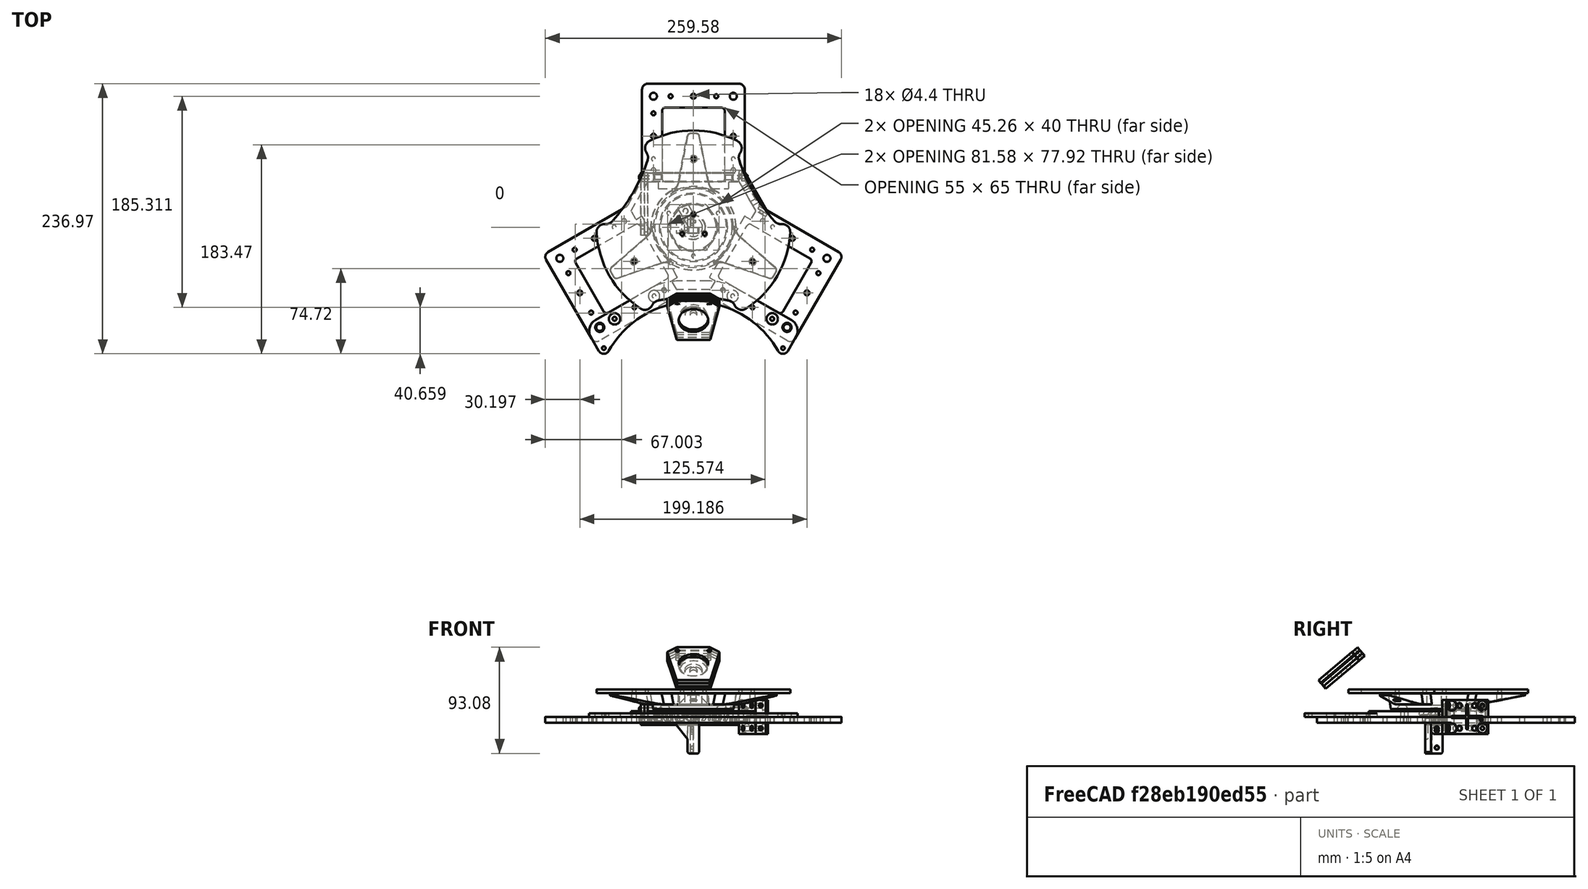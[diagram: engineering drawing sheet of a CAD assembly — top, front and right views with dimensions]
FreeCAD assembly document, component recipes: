
FREECAD ASSEMBLY — COMPONENT RECIPES ("structures")

This assembly document has 14 components, labeled P0..P13 below (a component is one placed body or linked part). 12 of them carry a construction recipe — the FreeCAD feature program that regenerates the part from scratch, quoted from this document or its linked companion documents; the rest are supplied as boundary geometry only. No exploded tour is included for this assembly.
NOTE — this tour is split across 2 documents so each fits a 32k-token context. This is document 1: the component sections continue in the remaining 1 document, each repeating the header above.
COMPONENT P0 — recipe-attached ("PlaqueIntermediaire", modeled in this document).
Construction recipe (the document's own serialized feature program — sketch geometry with constraints, then the solid features built on it; lengths are millimeters unless a unit is written):

FEATURE [Sketcher::SketchObject] Sketch043
  ArcFitTolerance = 0
  AttachmentSupport = -> [XY_Plane031]
  ExternalBSplineMaxDegree = 0
  ExternalBSplineTolerance = 0
  FullyConstrained = true
  InternalTolerance = 1e-06
  InvalidShape = false
  MakeInternals = false
  MapMode = 5
  Support = -> [XY_Plane031]
  TreeRank = 0
  ValidateShape = true
  sketch-geometry (13):
    g0: LineSegment StartX=0 StartY=0 StartZ=0 EndX=0 EndY=-54.641 EndZ=0
    g1: LineSegment StartX=0 StartY=-54.641 StartZ=0 EndX=-14.641 EndY=-54.641 EndZ=0
    g2: LineSegment StartX=-14.641 StartY=-54.641 StartZ=0 EndX=-19.641 EndY=-45.9808 EndZ=0
    g3: LineSegment StartX=-19.641 StartY=-45.9808 StartZ=0 EndX=-28.3013 EndY=-50.9808 EndZ=0
    g4: LineSegment StartX=-28.3013 StartY=-50.9808 StartZ=0 EndX=-58.3013 EndY=0.980762 EndZ=0
    g5: LineSegment StartX=-58.3013 StartY=0.980762 StartZ=0 EndX=-49.641 EndY=5.98076 EndZ=0
    g6: LineSegment StartX=-49.641 StartY=5.98076 StartZ=0 EndX=-54.641 EndY=14.641 EndZ=0
    g7: LineSegment StartX=-54.641 StartY=14.641 StartZ=0 EndX=-47.3205 EndY=27.3205 EndZ=0
    g8: LineSegment StartX=-47.3205 StartY=27.3205 StartZ=0 EndX=0 EndY=0 EndZ=0
    g9: LineSegment [constr] StartX=-49.641 StartY=5.98076 StartZ=0 EndX=-19.641 EndY=-45.9808 EndZ=0
    g10: Circle CenterX=-43.4808 CenterY=15.3109 CenterZ=0 NormalX=0 NormalY=0 NormalZ=1 AngleXU=0 Radius=1.6
    g11: Circle CenterX=-8.48076 CenterY=-45.3109 CenterZ=0 NormalX=0 NormalY=0 NormalZ=1 AngleXU=0 Radius=1.6
    g12: LineSegment [constr] StartX=0 StartY=0 StartZ=0 EndX=-43.3013 EndY=-25 EndZ=0
  constraints (35):
    c: Coincident(g0,g-1)
    c: PointOnObject(g0,g-2)
    c: Coincident(g1,g0)
    c: Horizontal(g1)
    c: Coincident(g1,g2)
    c: Coincident(g2,g3)
    c: Coincident(g3,g4)
    c: Coincident(g4,g5)
    c: Coincident(g5,g6)
    c: Coincident(g6,g7)
    c: Coincident(g7,g8)
    c: Coincident(g8,g0)
    c: Angle(g8,g0) = 2.0944
    c: Perpendicular(g7,g8)
    c: Perpendicular(g3,g2)
    c: Perpendicular(g4,g3)
    c: Perpendicular(g4,g5)
    c: Perpendicular(g6,g5)
    c: Equal(g7,g1)
    c: Coincident(g9,g5)
    c: Tangent(g9,g2) = 1.5708
    c: Equal(g2,g3)
    c: Equal(g5,g6)
    c: Distance(g6) = 10
    c: Equal(g0,g8)
    c: Distance(g4) = 60
    c: Distance(g0,g9) = 40
    c: Coincident(g12,g0)
    c: PointOnObject(g12,g4)
    c: Perpendicular(g4,g12)
    c: Symmetric(g11,g10,g12)
    c: Diameter(g10) = 3.2
    c: Equal(g10,g11)
    c: Distance(g11,g2) = 10
    c: Distance(g11,g12) = 35
FEATURE [PartDesign::Pad] Pad027
  AddSubType = 0
  AutoTaperInnerAngle = false
  CheckUpToFaceLimits = true
  ClaimChildren = false
  Direction = (1,1,1)
  Fit = 0
  FitJoin = 0
  InnerFit = 0
  InnerFitJoin = 0
  InvalidShape = false
  Length = 5
  Length2 = 100
  Linearize = true
  NewSolid = false
  Profile = -> Sketch043
  Refine = true
  Suppress = false
  TaperInnerAngle = 0
  TaperInnerAngleRev = 0
  TreeRank = 0
  Type = 0
  ValidateShape = true
  _ProfileBasedVersion = 1
FEATURE [PartDesign::PolarPattern] PolarPattern014
  AddSubType = 0
  Angle = 360
  Axis = -> Sketch043 [N_Axis]
  BaseFeature = -> Pad027
  CopyShape = false
  InvalidShape = false
  NewSolid = false
  Occurrences = 3
  OriginalSubs = -> [Pad027]
  Originals = -> [Pad027]
  ParallelTransform = true
  Refine = true
  SubTransform = true
  Suppress = false
  TreeRank = 0
  ValidateShape = true
  _Version = 2
FEATURE [Sketcher::SketchObject] Sketch044
  ArcFitTolerance = 0
  AttachmentSupport = -> [XY_Plane031]
  ExternalBSplineMaxDegree = 0
  ExternalBSplineTolerance = 0
  FullyConstrained = true
  InternalTolerance = 1e-06
  InvalidShape = false
  MakeInternals = false
  MapMode = 5
  Support = -> [XY_Plane031]
  TreeRank = 0
  ValidateShape = true
  sketch-geometry (5):
    g0: LineSegment StartX=-35.6218 StartY=8.30127 StartZ=0 EndX=-10.6218 EndY=-35 EndZ=0
    g1: LineSegment StartX=-10.6218 StartY=-35 StartZ=0 EndX=0 EndY=-35 EndZ=0
    g2: LineSegment StartX=0 StartY=-35 StartZ=0 EndX=0 EndY=0 EndZ=0
    g3: LineSegment StartX=0 StartY=0 StartZ=0 EndX=-30.3109 EndY=17.5 EndZ=0
    g4: LineSegment StartX=-30.3109 StartY=17.5 StartZ=0 EndX=-35.6218 EndY=8.30127 EndZ=0
  constraints (14):
    c: Coincident(g0,g1)
    c: PointOnObject(g1,g-2)
    c: Horizontal(g1)
    c: Coincident(g1,g2)
    c: Coincident(g2,g-1)
    c: Coincident(g2,g3)
    c: Coincident(g3,g4)
    c: Coincident(g4,g0)
    c: Perpendicular(g4,g3)
    c: Equal(g4,g1)
    c: Equal(g2,g3)
    c: Angle(g3,g2) = 2.0944
    c: Distance(g0) = 50
    c: DistanceY(g2,g2) = 35
FEATURE [PartDesign::Pocket] Pocket017
  AddSubType = 1
  AutoTaperInnerAngle = false
  BaseFeature = -> PolarPattern014
  CheckUpToFaceLimits = true
  ClaimChildren = false
  Direction = (1,1,1)
  Fit = 0
  FitJoin = 0
  InnerFit = 0
  InnerFitJoin = 0
  InvalidShape = false
  Length = 5
  Length2 = 100
  Linearize = true
  NewSolid = false
  Profile = -> Sketch044
  Refine = true
  Reversed = true
  Suppress = false
  TaperInnerAngle = 0
  TaperInnerAngleRev = 0
  TreeRank = 0
  Type = 1
  ValidateShape = true
  _ProfileBasedVersion = 1
  _Version = 0
FEATURE [PartDesign::PolarPattern] PolarPattern015
  AddSubType = 0
  Angle = 360
  Axis = -> Sketch044 [N_Axis]
  BaseFeature = -> Pocket017
  CopyShape = false
  InvalidShape = false
  NewSolid = false
  Occurrences = 3
  OriginalSubs = -> [Pocket017]
  Originals = -> [Pocket017]
  ParallelTransform = true
  Refine = true
  SubTransform = true
  Suppress = false
  TreeRank = 0
  ValidateShape = true
  _Version = 2
FEATURE [PartDesign::Chamfer] Chamfer007
  AddSubType = 0
  Angle = 45
  Base = -> PolarPattern015 [Edge8,Edge66,Edge67,Edge68,Edge77,Edge78]
  BaseFeature = -> PolarPattern015
  ChamferType = 0
  FlipDirection = false
  InvalidShape = false
  NewSolid = false
  Refine = true
  Size = 1
  Size2 = 1
  SupportTransform = false
  Suppress = false
  TreeRank = 0
  UseAllEdges = false
  ValidateShape = true
FEATURE [PartDesign::Fillet] Fillet014
  AddSubType = 0
  Base = -> Chamfer007 [Edge101,Edge103,Edge104,Edge105,Edge106,Edge102]
  BaseFeature = -> Chamfer007
  InvalidShape = false
  NewSolid = false
  Radius = 3
  Refine = true
  SupportTransform = false
  Suppress = false
  TreeRank = 0
  UseAllEdges = false
  ValidateShape = true
FEATURE [PartDesign::Body] Body024  label="PlaqueIntermediaire"
  AutoGroupSolids = false
  ClaimAllChildren = false
  ExportMode = 0
  Group = -> [Sketch043,Pad027,PolarPattern014,Sketch044,Pocket017,PolarPattern015,Chamfer007,Fillet014]
  InvalidShape = false
  Origin = -> Origin036
  SingleSolid = true
  Tip = -> Fillet014
  TreeRank = 0
  ValidateShape = true
  _ExportChildren = -> [Pad027,PolarPattern014,Pocket017,PolarPattern015,Chamfer007,Fillet014]
  _GroupVersion = 1
COMPONENT P1 — recipe-attached ("CoinStandard", modeled in this document).
Construction recipe (the document's own serialized feature program — sketch geometry with constraints, then the solid features built on it; lengths are millimeters unless a unit is written):

FEATURE [Sketcher::SketchObject] Sketch060
  ArcFitTolerance = 0
  AttachmentSupport = -> [XY_Plane037]
  ExternalBSplineMaxDegree = 0
  ExternalBSplineTolerance = 0
  FullyConstrained = true
  InternalTolerance = 1e-06
  InvalidShape = false
  MakeInternals = false
  MapMode = 5
  Support = -> [XY_Plane037]
  TreeRank = 0
  ValidateShape = true
  sketch-geometry (10):
    g0: LineSegment [constr] StartX=0 StartY=0 StartZ=0 EndX=34.641 EndY=-20 EndZ=0
    g1: LineSegment [constr] StartX=0 StartY=0 StartZ=0 EndX=-34.641 EndY=-20 EndZ=0
    g2: LineSegment [constr] StartX=-34.641 StartY=-20 StartZ=0 EndX=-14.641 EndY=-54.641 EndZ=0
    g3: LineSegment [constr] StartX=34.641 StartY=-20 StartZ=0 EndX=14.641 EndY=-54.641 EndZ=0
    g4: LineSegment StartX=-14.641 StartY=-54.641 StartZ=0 EndX=-23.3013 EndY=-59.641 EndZ=0
    g5: LineSegment StartX=14.641 StartY=-54.641 StartZ=0 EndX=23.3013 EndY=-59.641 EndZ=0
    g6: LineSegment StartX=-23.3013 StartY=-59.641 StartZ=0 EndX=-15 EndY=-89.641 EndZ=0
    g7: LineSegment StartX=23.3013 StartY=-59.641 StartZ=0 EndX=15 EndY=-89.641 EndZ=0
    g8: LineSegment StartX=-14.641 StartY=-54.641 StartZ=0 EndX=14.641 EndY=-54.641 EndZ=0
    g9: LineSegment StartX=-15 StartY=-89.641 StartZ=0 EndX=15 EndY=-89.641 EndZ=0
  constraints (24):
    c: Coincident(g0,g-1)
    c: Coincident(g1,g0)
    c: Symmetric(g0,g1,g-2)
    c: Angle(g1,g0) = 2.0944
    c: Coincident(g2,g1)
    c: Perpendicular(g1,g2)
    c: Coincident(g3,g0)
    c: Symmetric(g3,g2,g-2)
    c: Distance(g2) = 40
    c: Distance(g0) = 40
    c: Coincident(g4,g2)
    c: Coincident(g5,g3)
    c: Perpendicular(g3,g5)
    c: Symmetric(g4,g5,g-2)
    c: Distance(g5) = 10
    c: Coincident(g6,g4)
    c: Coincident(g7,g5)
    c: Symmetric(g7,g6,g-2)
    c: DistanceY(g7,g3) = 35
    c: Coincident(g8,g4)
    c: Coincident(g8,g5)
    c: Coincident(g9,g6)
    c: Coincident(g9,g7)
    c: DistanceX(g9,g9) = 30
FEATURE [PartDesign::Pad] Pad034
  AddSubType = 0
  AutoTaperInnerAngle = false
  CheckUpToFaceLimits = true
  ClaimChildren = false
  Direction = (1,1,1)
  Fit = 0
  FitJoin = 0
  InnerFit = 0
  InnerFitJoin = 0
  InvalidShape = false
  Length = 50
  Length2 = 100
  Linearize = true
  NewSolid = false
  Profile = -> Sketch060
  Refine = true
  Suppress = false
  TaperInnerAngle = 0
  TaperInnerAngleRev = 0
  TreeRank = 0
  Type = 0
  ValidateShape = true
  _ProfileBasedVersion = 1
FEATURE [Sketcher::SketchObject] Sketch061
  ArcFitTolerance = 0
  AttachmentSupport = -> [YZ_Plane037]
  ExternalBSplineMaxDegree = 0
  ExternalBSplineTolerance = 0
  ExternalGeometry = -> [Pad034]
  FullyConstrained = true
  InternalTolerance = 1e-06
  InvalidShape = false
  MakeInternals = false
  MapMode = 5
  Placement = pos=(0,0,0) rot=(0.57735,0.57735,0.57735;2.0944rad)
  Support = -> [YZ_Plane037]
  TreeRank = 0
  ValidateShape = true
  sketch-geometry (4):
    g0: LineSegment StartX=-62.641 StartY=0 StartZ=0 EndX=-89.641 EndY=20.6315 EndZ=0
    g1: LineSegment StartX=-62.641 StartY=0 StartZ=0 EndX=-89.641 EndY=0 EndZ=0
    g2: LineSegment StartX=-89.641 StartY=0 StartZ=0 EndX=-89.641 EndY=20.6315 EndZ=0
    g3: LineSegment [constr] StartX=-89.641 StartY=20.6315 StartZ=0 EndX=-54.641 EndY=50 EndZ=0
  constraints (11):
    c: PointOnObject(g0,g-4)
    c: PointOnObject(g0,g-1)
    c: DistanceX(g0,g-3) = 3
    c: Coincident(g0,g1)
    c: PointOnObject(g1,g-4)
    c: Horizontal(g1)
    c: Coincident(g1,g2)
    c: Coincident(g2,g0)
    c: Coincident(g3,g0)
    c: Coincident(g3,g-5)
    c: Angle(g-4,g3) = 2.26893
FEATURE [PartDesign::Pocket] Pocket025
  AddSubType = 1
  AutoTaperInnerAngle = false
  BaseFeature = -> Pad034
  CheckUpToFaceLimits = true
  ClaimChildren = false
  Direction = (1,1,1)
  Fit = 0
  FitJoin = 0
  InnerFit = 0
  InnerFitJoin = 0
  InvalidShape = false
  Length = 5
  Length2 = 100
  Linearize = true
  Midplane = true
  NewSolid = false
  Profile = -> Sketch061
  Refine = true
  Suppress = false
  TaperInnerAngle = 0
  TaperInnerAngleRev = 0
  TreeRank = 0
  Type = 1
  ValidateShape = true
  _ProfileBasedVersion = 1
  _Version = 1
FEATURE [Sketcher::SketchObject] Sketch062
  ArcFitTolerance = 0
  AttachmentSupport = -> [YZ_Plane037]
  ExternalBSplineMaxDegree = 0
  ExternalBSplineTolerance = 0
  ExternalGeometry = -> [Pocket025]
  FullyConstrained = true
  InternalTolerance = 1e-06
  InvalidShape = false
  MakeInternals = false
  MapMode = 5
  Placement = pos=(0,0,0) rot=(0.57735,0.57735,0.57735;2.0944rad)
  Support = -> [YZ_Plane037]
  TreeRank = 0
  ValidateShape = true
  sketch-geometry (3):
    g0: LineSegment StartX=-89.641 StartY=50 StartZ=0 EndX=-89.641 EndY=20.6315 EndZ=0
    g1: LineSegment StartX=-89.641 StartY=20.6315 StartZ=0 EndX=-54.641 EndY=50 EndZ=0
    g2: LineSegment StartX=-89.641 StartY=50 StartZ=0 EndX=-54.641 EndY=50 EndZ=0
  constraints (6):
    c: Coincident(g1,g0)
    c: Coincident(g-3,g0)
    c: Coincident(g-3,g0)
    c: Coincident(g2,g0)
    c: Coincident(g2,g1)
    c: Coincident(g1,g-5)
FEATURE [PartDesign::Pocket] Pocket026
  AddSubType = 1
  AutoTaperInnerAngle = false
  BaseFeature = -> Pocket025
  CheckUpToFaceLimits = true
  ClaimChildren = false
  Direction = (1,1,1)
  Fit = 0
  FitJoin = 0
  InnerFit = 0
  InnerFitJoin = 0
  InvalidShape = false
  Length = 5
  Length2 = 100
  Linearize = true
  Midplane = true
  NewSolid = false
  Profile = -> Sketch062
  Refine = true
  Suppress = false
  TaperInnerAngle = 0
  TaperInnerAngleRev = 0
  TreeRank = 0
  Type = 1
  ValidateShape = true
  _ProfileBasedVersion = 1
  _Version = 1
FEATURE [PartDesign::Plane] DatumPlane
  AttachmentOffset = pos=(0,0,-30) rot=(0,0,1;0rad)
  AttachmentSupport = -> [Pocket026]
  InvalidShape = false
  Length = 68.3013
  MapMode = 5
  MinimumLength = 10
  MinimumWidth = 10
  Placement = pos=(-35,-60.6218,3.3e-15) rot=(0.186157,0.694747,0.694747;2.77349rad)
  ResizeMode = 0
  Support = -> [Pocket026]
  TreeRank = 0
  ValidateShape = true
  Width = 10
FEATURE [Sketcher::SketchObject] Sketch063
  ArcFitTolerance = 0
  AttachmentSupport = -> [DatumPlane]
  ExternalBSplineMaxDegree = 0
  ExternalBSplineTolerance = 0
  ExternalGeometry = -> [Pocket026]
  FullyConstrained = true
  InternalTolerance = 1e-06
  InvalidShape = false
  MakeInternals = false
  MapMode = 5
  Placement = pos=(-35,-60.6218,3.3e-15) rot=(0.186157,0.694747,0.694747;2.77349rad)
  Support = -> [DatumPlane]
  TreeRank = 0
  ValidateShape = true
  sketch-geometry (2):
    g0: Circle CenterX=-45 CenterY=10 CenterZ=0 NormalX=0 NormalY=0 NormalZ=1 AngleXU=0 Radius=1.6
    g1: LineSegment [constr] StartX=-50 StartY=10 StartZ=0 EndX=-40 EndY=10 EndZ=0
  constraints (6):
    c: PointOnObject(g1,g-3)
    c: PointOnObject(g1,g-4)
    c: Horizontal(g1)
    c: Symmetric(g1,g1,g0)
    c: Diameter(g0) = 3.2
    c: Distance(g-3,g1) = 10
FEATURE [PartDesign::Hole] Hole001
  AddSubType = 1
  BaseFeature = -> Pocket026
  ClaimChildren = false
  CustomThreadClearance = 0
  Depth = 39
  DepthType = 0
  Diameter = 3.2
  DrillForDepth = false
  DrillPoint = 1
  DrillPointAngle = 118
  Fit = 0
  FitJoin = 0
  HoleCutCountersinkAngle = 90
  HoleCutCustomValues = true
  HoleCutDepth = 27
  HoleCutDiameter = 8
  HoleCutType = 1
  InnerFit = 0
  InnerFitJoin = 0
  InvalidShape = false
  ModelThread = false
  NewSolid = false
  Profile = -> Sketch063
  Refine = true
  Reversed = true
  Suppress = false
  Tapered = false
  TaperedAngle = 90
  ThreadClass = 0
  ThreadDepth = 39
  ThreadDepthType = 0
  ThreadDirection = 0
  ThreadFit = 0
  ThreadSize = 0
  ThreadType = 0
  Threaded = false
  TreeRank = 0
  UseCustomThreadClearance = false
  ValidateShape = true
  _ProfileBasedVersion = 1
FEATURE [PartDesign::Mirrored] Mirrored006
  AddSubType = 0
  BaseFeature = -> Hole001
  CopyShape = false
  InvalidShape = false
  MirrorPlane = -> YZ_Plane037
  NewSolid = false
  OriginalSubs = -> [Hole001]
  Originals = -> [Hole001]
  ParallelTransform = true
  Refine = true
  SubTransform = true
  Suppress = false
  TreeRank = 0
  ValidateShape = true
  _Version = 3
FEATURE [Sketcher::SketchObject] Sketch064
  ArcFitTolerance = 0
  AttachmentSupport = -> [Mirrored006]
  ExternalBSplineMaxDegree = 0
  ExternalBSplineTolerance = 0
  ExternalGeometry = -> [Mirrored006]
  FullyConstrained = true
  InternalTolerance = 1e-06
  InvalidShape = false
  MakeInternals = false
  MapMode = 5
  Placement = pos=(-2.64e-14,-47.1965,56.2467) rot=(1,0,0;0.698132rad)
  Support = -> [Mirrored006]
  TreeRank = 0
  ValidateShape = true
  sketch-geometry (2):
    g0: Circle CenterX=-14 CenterY=-14.7181 CenterZ=0 NormalX=0 NormalY=0 NormalZ=1 AngleXU=0 Radius=2.05
    g1: Circle CenterX=14 CenterY=-14.7181 CenterZ=0 NormalX=0 NormalY=0 NormalZ=1 AngleXU=0 Radius=2.05
  constraints (5):
    c: Symmetric(g1,g0,g-2)
    c: Diameter(g0) = 4.1
    c: Equal(g0,g1)
    c: DistanceX(g0,g1) = 28
    c: DistanceY(g0,g-3) = 5
FEATURE [PartDesign::Pocket] Pocket027
  AddSubType = 1
  AutoTaperInnerAngle = false
  BaseFeature = -> Mirrored006
  CheckUpToFaceLimits = true
  ClaimChildren = false
  Direction = (1,1,1)
  Fit = 0
  FitJoin = 0
  InnerFit = 0
  InnerFitJoin = 0
  InvalidShape = false
  Length = 5
  Length2 = 100
  Linearize = true
  NewSolid = false
  Profile = -> Sketch064
  Refine = true
  Suppress = false
  TaperInnerAngle = 0
  TaperInnerAngleRev = 0
  TreeRank = 0
  Type = 1
  ValidateShape = true
  _ProfileBasedVersion = 1
  _Version = 1
FEATURE [Sketcher::SketchObject] Sketch065
  ArcFitTolerance = 0
  AttachmentSupport = -> [Pocket027]
  ExternalBSplineMaxDegree = 0
  ExternalBSplineTolerance = 0
  ExternalGeometry = -> [Pocket027]
  FullyConstrained = true
  InternalTolerance = 1e-06
  InvalidShape = false
  MakeInternals = false
  MapMode = 5
  Placement = pos=(-2.64e-14,-47.1965,56.2467) rot=(1,0,0;0.698132rad)
  Support = -> [Pocket027]
  TreeRank = 0
  ValidateShape = true
  sketch-geometry (3):
    g0: Circle CenterX=0 CenterY=-32.5627 CenterZ=0 NormalX=0 NormalY=0 NormalZ=1 AngleXU=0 Radius=15
    g1: GeomPoint [constr] X=2e-16 Y=-55.4073 Z=0
    g2: GeomPoint [constr] X=0 Y=-9.71807 Z=0
  constraints (6):
    c: PointOnObject(g0,g-2)
    c: Diameter(g0) = 30
    c: PointOnObject(g2,g-2)
    c: PointOnObject(g2,g-3)
    c: PointOnObject(g1,g-4)
    c: Symmetric(g1,g2,g0)
FEATURE [PartDesign::Pocket] Pocket028
  AddSubType = 1
  AutoTaperInnerAngle = false
  BaseFeature = -> Pocket027
  CheckUpToFaceLimits = true
  ClaimChildren = false
  Direction = (1,1,1)
  Fit = 0
  FitJoin = 0
  InnerFit = 0
  InnerFitJoin = 0
  InvalidShape = false
  Length = 17
  Length2 = 100
  Linearize = true
  NewSolid = false
  Profile = -> Sketch065
  Refine = true
  Suppress = false
  TaperInnerAngle = 0
  TaperInnerAngleRev = 0
  TreeRank = 0
  Type = 0
  ValidateShape = true
  _ProfileBasedVersion = 1
  _Version = 1
FEATURE [Sketcher::SketchObject] Sketch066
  ArcFitTolerance = 0
  AttachmentSupport = -> [Pocket028]
  ExternalBSplineMaxDegree = 0
  ExternalBSplineTolerance = 0
  ExternalGeometry = -> [Pocket028]
  FullyConstrained = true
  InternalTolerance = 1e-06
  InvalidShape = false
  MakeInternals = false
  MapMode = 5
  Placement = pos=(-2.64e-14,-47.1965,56.2467) rot=(1,0,0;0.698132rad)
  Support = -> [Pocket028]
  TreeRank = 0
  ValidateShape = true
  sketch-geometry (4):
    g0: ArcOfCircle CenterX=0 CenterY=-32.5627 CenterZ=0 NormalX=0 NormalY=0 NormalZ=1 AngleXU=0 Radius=11.5 StartAngle=3.22982 EndAngle=6.19496
    g1: LineSegment StartX=-11.4553 StartY=-33.576 StartZ=0 EndX=-12.3039 EndY=-23.9828 EndZ=0
    g2: LineSegment StartX=12.3039 StartY=-23.9828 StartZ=0 EndX=11.4553 EndY=-33.576 EndZ=0
    g3: LineSegment StartX=-12.3039 StartY=-23.9828 StartZ=0 EndX=12.3039 EndY=-23.9828 EndZ=0
  constraints (8):
    c: Coincident(g0,g-3)
    c: Diameter(g0) = 23
    c: Coincident(g1,g-4)
    c: Coincident(g2,g-4)
    c: Coincident(g3,g1)
    c: Coincident(g3,g2)
    c: Tangent(g1,g0) = 1.5708
    c: Tangent(g2,g0) = 1.5708
FEATURE [PartDesign::Pocket] Pocket029
  AddSubType = 1
  AutoTaperInnerAngle = false
  BaseFeature = -> Pocket028
  CheckUpToFaceLimits = true
  ClaimChildren = false
  Direction = (1,1,1)
  Fit = 0
  FitJoin = 0
  InnerFit = 0
  InnerFitJoin = 0
  InvalidShape = false
  Length = 5
  Length2 = 100
  Linearize = true
  NewSolid = false
  Profile = -> Sketch066
  Refine = true
  Suppress = false
  TaperInnerAngle = 0
  TaperInnerAngleRev = 0
  TreeRank = 0
  Type = 1
  ValidateShape = true
  _ProfileBasedVersion = 1
  _Version = 1
FEATURE [PartDesign::Chamfer] Chamfer018
  AddSubType = 0
  Angle = 45
  Base = -> Pocket029 [Edge44,Edge31]
  BaseFeature = -> Pocket029
  ChamferType = 0
  FlipDirection = false
  InvalidShape = false
  NewSolid = false
  Refine = true
  Size = 0.4
  Size2 = 1
  SupportTransform = false
  Suppress = false
  TreeRank = 0
  UseAllEdges = false
  ValidateShape = true
FEATURE [PartDesign::Pad] Pad036
  AddSubType = 0
  AutoTaperInnerAngle = false
  BaseFeature = -> Chamfer018
  CheckUpToFaceLimits = true
  ClaimChildren = false
  Direction = (1,1,1)
  Fit = 0
  FitJoin = 0
  InnerFit = 0
  InnerFitJoin = 0
  InvalidShape = false
  Length = 5
  Length2 = 100
  Linearize = true
  NewSolid = false
  Profile = -> Chamfer018 [Face5]
  Refine = true
  Suppress = false
  TaperInnerAngle = 0
  TaperInnerAngleRev = 0
  TreeRank = 0
  Type = 0
  ValidateShape = true
  _ProfileBasedVersion = 1
FEATURE [PartDesign::Chamfer] Chamfer022
  AddSubType = 0
  Angle = 45
  Base = -> Pad036 [Face15]
  BaseFeature = -> Pad036
  ChamferType = 0
  FlipDirection = false
  InvalidShape = false
  NewSolid = false
  Refine = true
  Size = 0.4
  Size2 = 1
  SupportTransform = false
  Suppress = false
  TreeRank = 0
  UseAllEdges = false
  ValidateShape = true
FEATURE [PartDesign::Chamfer] Chamfer023
  AddSubType = 0
  Angle = 45
  Base = -> Chamfer022 [Edge64,Edge63]
  BaseFeature = -> Chamfer022
  ChamferType = 0
  FlipDirection = false
  InvalidShape = false
  NewSolid = false
  Refine = true
  Size = 1
  Size2 = 1
  SupportTransform = false
  Suppress = false
  TreeRank = 0
  UseAllEdges = false
  ValidateShape = true
FEATURE [PartDesign::Body] Body029  label="CoinStandard"
  AutoGroupSolids = false
  ClaimAllChildren = false
  ExportMode = 0
  Group = -> [Sketch060,Pad034,Sketch061,Pocket025,Sketch062,Pocket026,DatumPlane,Sketch063,Hole001,Mirrored006,Sketch064,Pocket027,Sketch065,Pocket028,Sketch066,Pocket029,Chamfer018,Pad036,Chamfer022,Chamfer023]
  InvalidShape = false
  Origin = -> Origin046
  SingleSolid = true
  Tip = -> Chamfer023
  TreeRank = 0
  ValidateShape = true
  _ExportChildren = -> [Pad034,Pocket025,Pocket026,DatumPlane,Hole001,Mirrored006,Pocket027,Pocket028,Pocket029,Chamfer018,Pad036,Chamfer022,Chamfer023]
  _GroupVersion = 1
COMPONENT P2 — recipe-attached ("Link075(Semelle)", modeled in this document).
Construction recipe (the document's own serialized feature program — sketch geometry with constraints, then the solid features built on it; lengths are millimeters unless a unit is written):

FEATURE [Sketcher::SketchObject] Sketch032
  ArcFitTolerance = 0
  AttachmentSupport = -> [XY_Plane026]
  ExternalBSplineMaxDegree = 0
  ExternalBSplineTolerance = 0
  FullyConstrained = true
  InternalTolerance = 1e-06
  InvalidShape = false
  MakeInternals = false
  MapMode = 5
  Support = -> [XY_Plane026]
  TreeRank = 0
  ValidateShape = true
  sketch-geometry (56):
    g0: LineSegment StartX=-131.619 StartY=-24.0289 StartZ=0 EndX=-58.007 EndY=18.4711 EndZ=0
    g1: LineSegment StartX=-58.007 StartY=18.4711 StartZ=0 EndX=-45 EndY=41 EndZ=0
    g2: LineSegment StartX=-45 StartY=41 StartZ=0 EndX=-45 EndY=126 EndZ=0
    g3: LineSegment StartX=-45 StartY=126 StartZ=0 EndX=45 EndY=126 EndZ=0
    g4: LineSegment StartX=45 StartY=126 StartZ=0 EndX=45 EndY=41 EndZ=0
    g5: LineSegment StartX=45 StartY=41 StartZ=0 EndX=58.007 EndY=18.4711 EndZ=0
    g6: LineSegment StartX=58.007 StartY=18.4711 StartZ=0 EndX=131.619 EndY=-24.0289 EndZ=0
    g7: LineSegment StartX=131.619 StartY=-24.0289 StartZ=0 EndX=86.6192 EndY=-101.971 EndZ=0
    g8: LineSegment StartX=86.6192 StartY=-101.971 StartZ=0 EndX=13.007 EndY=-59.4711 EndZ=0
    g9: LineSegment StartX=13.007 StartY=-59.4711 StartZ=0 EndX=-13.007 EndY=-59.4711 EndZ=0
    g10: LineSegment StartX=-13.007 StartY=-59.4711 StartZ=0 EndX=-86.6192 EndY=-101.971 EndZ=0
    g11: LineSegment StartX=-86.6192 StartY=-101.971 StartZ=0 EndX=-131.619 EndY=-24.0289 EndZ=0
    g12: LineSegment [constr] StartX=-1e-16 StartY=1e-16 StartZ=0 EndX=-1e-16 EndY=126 EndZ=0
    g13: LineSegment [constr] StartX=-1e-16 StartY=1e-16 StartZ=0 EndX=-109.119 EndY=-63 EndZ=0
    g14: LineSegment [constr] StartX=-1e-16 StartY=1e-16 StartZ=0 EndX=109.119 EndY=-63 EndZ=0
    g15: LineSegment StartX=-27.5 StartY=40 StartZ=0 EndX=27.5 EndY=40 EndZ=0
    g16: LineSegment StartX=27.5 StartY=40 StartZ=0 EndX=27.5 EndY=105 EndZ=0
    g17: LineSegment StartX=27.5 StartY=105 StartZ=0 EndX=-27.5 EndY=105 EndZ=0
    g18: LineSegment StartX=-27.5 StartY=105 StartZ=0 EndX=-27.5 EndY=40 EndZ=0
    g19: LineSegment StartX=20.891 StartY=-43.8157 StartZ=0 EndX=48.391 EndY=3.8157 EndZ=0
    g20: LineSegment StartX=48.391 StartY=3.8157 StartZ=0 EndX=104.683 EndY=-28.6843 EndZ=0
    g21: LineSegment StartX=104.683 StartY=-28.6843 StartZ=0 EndX=77.1827 EndY=-76.3157 EndZ=0
    g22: LineSegment StartX=77.1827 StartY=-76.3157 StartZ=0 EndX=20.891 EndY=-43.8157 EndZ=0
    g23: LineSegment StartX=-104.683 StartY=-28.6843 StartZ=0 EndX=-77.1827 EndY=-76.3157 EndZ=0
    g24: LineSegment StartX=-77.1827 StartY=-76.3157 StartZ=0 EndX=-20.891 EndY=-43.8157 EndZ=0
    g25: LineSegment StartX=-20.891 StartY=-43.8157 StartZ=0 EndX=-48.391 EndY=3.8157 EndZ=0
    g26: LineSegment StartX=-48.391 StartY=3.8157 StartZ=0 EndX=-104.683 EndY=-28.6843 EndZ=0
    g27: Circle [constr] CenterX=-1e-16 CenterY=1e-16 CenterZ=0 NormalX=0 NormalY=0 NormalZ=1 AngleXU=0 Radius=48.5412
    g28: LineSegment StartX=-11.547 StartY=-20 StartZ=0 EndX=-23.094 EndY=0 EndZ=0
    g29: LineSegment StartX=-23.094 StartY=-1.3e-15 StartZ=0 EndX=-11.547 EndY=20 EndZ=0
    g30: LineSegment StartX=-11.547 StartY=20 StartZ=0 EndX=11.547 EndY=20 EndZ=0
    g31: LineSegment StartX=11.547 StartY=20 StartZ=0 EndX=23.094 EndY=0 EndZ=0
    g32: LineSegment StartX=23.094 StartY=9e-16 StartZ=0 EndX=11.547 EndY=-20 EndZ=0
    g33: LineSegment StartX=11.547 StartY=-20 StartZ=0 EndX=-11.547 EndY=-20 EndZ=0
    g34: Circle [constr] CenterX=-1e-16 CenterY=1e-16 CenterZ=0 NormalX=0 NormalY=0 NormalZ=1 AngleXU=0 Radius=23.094
    g35: Circle CenterX=-21.6506 CenterY=12.5 CenterZ=0 NormalX=0 NormalY=0 NormalZ=1 AngleXU=0 Radius=1.6
    g36: Circle CenterX=21.6506 CenterY=12.5 CenterZ=0 NormalX=0 NormalY=0 NormalZ=1 AngleXU=0 Radius=1.6
    g37: Circle CenterX=0 CenterY=-25 CenterZ=0 NormalX=0 NormalY=0 NormalZ=1 AngleXU=0 Radius=1.6
    g38: LineSegment [constr] StartX=0 StartY=-25 StartZ=0 EndX=-1e-16 EndY=0 EndZ=0
    g39: LineSegment [constr] StartX=-1e-16 StartY=1e-16 StartZ=0 EndX=21.6506 EndY=12.5 EndZ=0
    g40: LineSegment [constr] StartX=-1e-16 StartY=1e-16 StartZ=0 EndX=-21.6506 EndY=12.5 EndZ=0
    g41: LineSegment [constr] StartX=-45 StartY=126 StartZ=0 EndX=-131.619 EndY=-24.0289 EndZ=0
    g42: LineSegment [constr] StartX=-86.6192 StartY=-101.971 StartZ=0 EndX=86.6192 EndY=-101.971 EndZ=0
    g43: LineSegment [constr] StartX=131.619 StartY=-24.0289 StartZ=0 EndX=45 EndY=126 EndZ=0
    g44: LineSegment [constr] StartX=-45 StartY=126 StartZ=0 EndX=-55 EndY=108.679 EndZ=0
    g45: LineSegment [constr] StartX=-55 StartY=108.679 StartZ=0 EndX=-45 EndY=41 EndZ=0
    g46: LineSegment [constr] StartX=-58.007 StartY=18.4711 StartZ=0 EndX=-121.619 EndY=-6.70835 EndZ=0
    g47: LineSegment [constr] StartX=-121.619 StartY=-6.70835 StartZ=0 EndX=-131.619 EndY=-24.0289 EndZ=0
    g48: LineSegment [constr] StartX=-86.6192 StartY=-101.971 StartZ=0 EndX=-66.6192 EndY=-101.971 EndZ=0
    g49: LineSegment [constr] StartX=-66.6192 StartY=-101.971 StartZ=0 EndX=-13.007 EndY=-59.4711 EndZ=0
    g50: LineSegment [constr] StartX=13.007 StartY=-59.4711 StartZ=0 EndX=66.6192 EndY=-101.971 EndZ=0
    g51: LineSegment [constr] StartX=66.6192 StartY=-101.971 StartZ=0 EndX=86.6192 EndY=-101.971 EndZ=0
    g52: LineSegment [constr] StartX=131.619 StartY=-24.0289 StartZ=0 EndX=121.619 EndY=-6.70835 EndZ=0
    g53: LineSegment [constr] StartX=121.619 StartY=-6.70835 StartZ=0 EndX=58.007 EndY=18.4711 EndZ=0
    g54: LineSegment [constr] StartX=45 StartY=41 StartZ=0 EndX=55 EndY=108.679 EndZ=0
    g55: LineSegment [constr] StartX=55 StartY=108.679 StartZ=0 EndX=45 EndY=126 EndZ=0
  constraints (151):
    c: Coincident(g0,g1)
    c: Coincident(g1,g2)
    c: Vertical(g2)
    c: Coincident(g2,g3)
    c: Horizontal(g3)
    c: Coincident(g3,g4)
    c: Vertical(g4)
    c: Coincident(g4,g5)
    c: Coincident(g5,g6)
    c: Coincident(g6,g7)
    c: Coincident(g7,g8)
    c: Coincident(g8,g9)
    c: Horizontal(g9)
    c: Coincident(g9,g10)
    c: Coincident(g10,g11)
    c: Coincident(g11,g0)
    c: Parallel(g8,g6)
    c: Parallel(g10,g0)
    c: Equal(g4,g6)
    c: Equal(g6,g8)
    c: Equal(g8,g10)
    c: Equal(g10,g0)
    c: Equal(g0,g2)
    c: Perpendicular(g6,g7)
    c: Perpendicular(g11,g10)
    c: Coincident(g12,g-1)
    c: PointOnObject(g12,g3)
    c: Vertical(g12)
    c: Coincident(g13,g12)
    c: Coincident(g14,g12)
    c: Symmetric(g6,g7,g14)
    c: Symmetric(g10,g0,g13)
    c: Perpendicular(g13,g11)
    c: Perpendicular(g7,g14)
    c: DistanceX(g3,g3) = 90
    c: Equal(g9,g5)
    c: Equal(g5,g1)
    c: Angle(g14,g12) = 2.0944
    c: Angle(g12,g13) = 2.0944
    c: DistanceY(g12,g2) = 126
    c: DistanceX(g9,g9) = 26.0141
    c: Coincident(g15,g16)
    c: Coincident(g16,g17)
    c: Coincident(g17,g18)
    c: Coincident(g18,g15)
    c: Horizontal(g15)
    c: Vertical(g16)
    c: Vertical(g18)
    c: Symmetric(g16,g17,g12)
    c: DistanceX(g17,g17) = 55
    c: DistanceY(g16,g16) = 65
    c: Coincident(g19,g20)
    c: Coincident(g20,g21)
    c: Coincident(g21,g22)
    c: Coincident(g22,g19)
    c: Coincident(g23,g24)
    c: Coincident(g24,g25)
    c: Coincident(g25,g26)
    c: Coincident(g26,g23)
    c: Equal(g25,g23)
    c: Equal(g23,g19)
    c: Equal(g19,g21)
    c: Equal(g21,g15)
    c: Equal(g22,g20)
    c: Equal(g20,g16)
    c: Equal(g16,g26)
    c: Equal(g26,g24)
    c: Parallel(g24,g13)
    c: Parallel(g22,g14)
    c: Symmetric(g23,g23,g13)
    c: Symmetric(g21,g20,g14)
    c: Coincident(g27,g12)
    c: PointOnObject(g19,g27)
    c: PointOnObject(g24,g27)
    c: PointOnObject(g15,g27)
    c: Equal(g11,g7)
    c: Equal(g7,g3)
    c: Coincident(g28,g29)
    c: Coincident(g29,g30)
    c: Coincident(g30,g31)
    c: Coincident(g31,g32)
    c: Coincident(g32,g33)
    c: Coincident(g33,g28)
    c: Horizontal(g33)
    c: Horizontal(g30)
    c: Equal(g29,g30)
    c: Equal(g30,g31)
    c: Equal(g31,g32)
    c: Equal(g32,g33)
    c: Equal(g33,g28)
    c: Coincident(g34,g12)
    c: PointOnObject(g30,g34)
    c: PointOnObject(g31,g34)
    c: PointOnObject(g32,g34)
    c: PointOnObject(g28,g34)
    c: PointOnObject(g28,g34)
    c: DistanceY(g12,g30) = 20
    c: PointOnObject(g37,g-2)
    c: Equal(g37,g36)
    c: Equal(g36,g35)
    c: Diameter(g35) = 3.2
    c: Coincident(g38,g37)
    c: Coincident(g38,g12)
    c: Coincident(g39,g12)
    c: Coincident(g39,g36)
    c: Coincident(g40,g12)
    c: Coincident(g40,g35)
    c: Perpendicular(g29,g40)
    c: Perpendicular(g31,g39)
    c: Equal(g40,g38)
    c: Equal(g38,g39)
    c: DistanceY(g38,g38) = 25
    c: Coincident(g41,g3)
    c: Coincident(g41,g11)
    c: Coincident(g42,g11)
    c: Coincident(g42,g7)
    c: Coincident(g43,g7)
    c: Coincident(g43,g3)
    c: Coincident(g3,g44)
    c: PointOnObject(g44,g41)
    c: Coincident(g44,g45)
    c: Coincident(g45,g1)
    c: Coincident(g1,g46)
    c: PointOnObject(g46,g41)
    c: Coincident(g46,g47)
    c: Coincident(g47,g11)
    c: Coincident(g11,g48)
    c: Horizontal(g48)
    c: Coincident(g48,g49)
    c: Coincident(g49,g9)
    c: Coincident(g9,g50)
    c: PointOnObject(g50,g42)
    c: Coincident(g50,g51)
    c: Coincident(g51,g7)
    c: Coincident(g7,g52)
    c: PointOnObject(g52,g43)
    c: Coincident(g52,g53)
    c: Coincident(g53,g5)
    c: Coincident(g5,g54)
    c: PointOnObject(g54,g43)
    c: Coincident(g54,g55)
    c: Coincident(g55,g3)
    c: Equal(g55,g44)
    c: Equal(g44,g47)
    c: Equal(g47,g48)
    c: Equal(g48,g51)
    c: Equal(g55,g52)
    c: DistanceX(g48,g48) = 20
    c: DistanceY(g16) = 105
    c: DistanceY(g50,g12) = 101.971
    c: DistanceY(g4,g4) = 85
FEATURE [PartDesign::Pad] Pad020
  AddSubType = 0
  AutoTaperInnerAngle = false
  CheckUpToFaceLimits = true
  ClaimChildren = false
  Direction = (0,0,1)
  Fit = 0
  FitJoin = 0
  InnerFit = 0
  InnerFitJoin = 0
  InvalidShape = false
  Length = 5
  Length2 = 100
  Linearize = true
  NewSolid = false
  Profile = -> Sketch032
  Refine = true
  Reversed = true
  Suppress = false
  TaperInnerAngle = 0
  TaperInnerAngleRev = 0
  TreeRank = 0
  Type = 0
  ValidateShape = true
  _ProfileBasedVersion = 1
FEATURE [PartDesign::Fillet] Fillet008
  AddSubType = 0
  Base = -> Pad020 [Edge41,Edge44,Edge37,Edge38,Edge65,Edge62,Edge61,Edge68,Edge49,Edge50,Edge53,Edge56]
  BaseFeature = -> Pad020
  InvalidShape = false
  NewSolid = false
  Radius = 3
  Refine = true
  SupportTransform = false
  Suppress = false
  TreeRank = 0
  UseAllEdges = false
  ValidateShape = true
FEATURE [PartDesign::Fillet] Fillet009
  AddSubType = 0
  Base = -> Fillet008 [Edge110,Edge99,Edge107,Edge106,Edge102,Edge103]
  BaseFeature = -> Fillet008
  InvalidShape = false
  NewSolid = false
  Radius = 5
  Refine = true
  SupportTransform = false
  Suppress = false
  TreeRank = 0
  UseAllEdges = false
  ValidateShape = true
FEATURE [PartDesign::Fillet] Fillet010
  AddSubType = 0
  Base = -> Fillet009 [Edge53,Edge57,Edge67,Edge71,Edge77,Edge81]
  BaseFeature = -> Fillet009
  InvalidShape = false
  NewSolid = false
  Radius = 5
  Refine = true
  SupportTransform = false
  Suppress = false
  TreeRank = 0
  UseAllEdges = false
  ValidateShape = true
FEATURE [Sketcher::SketchObject] Sketch033
  ArcFitTolerance = 0
  AttachmentSupport = -> [XY_Plane026]
  ExternalBSplineMaxDegree = 0
  ExternalBSplineTolerance = 0
  FullyConstrained = true
  InternalTolerance = 1e-06
  InvalidShape = false
  MakeInternals = false
  MapMode = 5
  Support = -> [XY_Plane026]
  TreeRank = 0
  ValidateShape = true
  sketch-geometry (13):
    g0: Circle CenterX=-20 CenterY=115 CenterZ=0 NormalX=0 NormalY=0 NormalZ=1 AngleXU=0 Radius=1.75
    g1: Circle CenterX=20 CenterY=115 CenterZ=0 NormalX=0 NormalY=0 NormalZ=1 AngleXU=0 Radius=1.75
    g2: Circle CenterX=-35 CenterY=60 CenterZ=0 NormalX=0 NormalY=0 NormalZ=1 AngleXU=0 Radius=1.75
    g3: Circle CenterX=-35 CenterY=100 CenterZ=0 NormalX=0 NormalY=0 NormalZ=1 AngleXU=0 Radius=1.75
    g4: Circle CenterX=35 CenterY=100 CenterZ=0 NormalX=0 NormalY=0 NormalZ=1 AngleXU=0 Radius=1.75
    g5: Circle CenterX=35 CenterY=60 CenterZ=0 NormalX=0 NormalY=0 NormalZ=1 AngleXU=0 Radius=1.75
    g6: Circle CenterX=-35 CenterY=115 CenterZ=0 NormalX=0 NormalY=0 NormalZ=1 AngleXU=0 Radius=3.1
    g7: Circle CenterX=35 CenterY=115 CenterZ=0 NormalX=0 NormalY=0 NormalZ=1 AngleXU=0 Radius=3.1
    g8: Circle CenterX=-35 CenterY=80 CenterZ=0 NormalX=0 NormalY=0 NormalZ=1 AngleXU=0 Radius=2.2
    g9: Circle CenterX=35 CenterY=80 CenterZ=0 NormalX=0 NormalY=0 NormalZ=1 AngleXU=0 Radius=2.2
    g10: Circle CenterX=-35 CenterY=50 CenterZ=0 NormalX=0 NormalY=0 NormalZ=1 AngleXU=0 Radius=2.2
    g11: Circle CenterX=35 CenterY=50 CenterZ=0 NormalX=0 NormalY=0 NormalZ=1 AngleXU=0 Radius=2.2
    g12: Circle CenterX=-1.0206e-12 CenterY=115 CenterZ=0 NormalX=0 NormalY=0 NormalZ=1 AngleXU=0 Radius=2.2
  constraints (31):
    c: Equal(g0,g3)
    c: Equal(g3,g2)
    c: Equal(g2,g1)
    c: Equal(g1,g4)
    c: Equal(g4,g5)
    c: Diameter(g0) = 3.5
    c: Symmetric(g1,g0,g-2)
    c: Symmetric(g3,g4,g-2)
    c: Symmetric(g2,g5,g-2)
    c: Vertical(g3,g2)
    c: DistanceX(g3,g4) = 70
    c: DistanceX(g0,g1) = 40
    c: DistanceY(g4,g1) = 15
    c: DistanceY(g5,g4) = 40
    c: DistanceY(g-1,g1) = 115
    c: Symmetric(g7,g6,g-2)
    c: Horizontal(g6,g0)
    c: Diameter(g7) = 6.2
    c: Equal(g7,g6)
    c: Vertical(g7,g4)
    c: Equal(g9,g8)
    c: Symmetric(g8,g9,g-2)
    c: Symmetric(g5,g4,g9)
    c: Diameter(g9) = 4.4
    c: Symmetric(g1,g0,g12)
    c: Equal(g12,g11)
    c: Equal(g11,g10)
    c: Equal(g10,g9)
    c: Vertical(g11,g5)
    c: Symmetric(g11,g10,g-2)
    c: DistanceY(g11,g5) = 10
FEATURE [PartDesign::Pocket] Pocket012
  AddSubType = 1
  AutoTaperInnerAngle = false
  BaseFeature = -> Fillet010
  CheckUpToFaceLimits = true
  ClaimChildren = false
  Direction = (1,1,1)
  Fit = 0
  FitJoin = 0
  InnerFit = 0
  InnerFitJoin = 0
  InvalidShape = false
  Length = 5
  Length2 = 100
  Linearize = true
  NewSolid = false
  Profile = -> Sketch033
  Refine = true
  Suppress = false
  TaperInnerAngle = 0
  TaperInnerAngleRev = 0
  TreeRank = 0
  Type = 1
  ValidateShape = true
  _ProfileBasedVersion = 1
  _Version = 0
FEATURE [PartDesign::PolarPattern] PolarPattern013
  AddSubType = 0
  Angle = 360
  Axis = -> Sketch033 [N_Axis]
  BaseFeature = -> Pocket012
  CopyShape = false
  InvalidShape = false
  NewSolid = false
  Occurrences = 3
  OriginalSubs = -> [Pocket012]
  Originals = -> [Pocket012]
  ParallelTransform = true
  Refine = true
  SubTransform = true
  Suppress = false
  TreeRank = 0
  ValidateShape = true
  _Version = 0
FEATURE [PartDesign::Fillet] Fillet011
  AddSubType = 0
  Base = -> PolarPattern013 [Edge190,Edge189,Edge192,Edge196,Edge198,Edge194]
  BaseFeature = -> PolarPattern013
  InvalidShape = false
  NewSolid = false
  Radius = 3
  Refine = true
  SupportTransform = false
  Suppress = false
  TreeRank = 0
  UseAllEdges = false
  ValidateShape = true
FEATURE [PartDesign::Body] Body019  label="Semelle"
  AutoGroupSolids = false
  ClaimAllChildren = false
  ExportMode = 0
  Group = -> [Sketch032,Pad020,Fillet008,Fillet009,Fillet010,Sketch033,Pocket012,PolarPattern013,Fillet011]
  InvalidShape = false
  Origin = -> Origin029
  SingleSolid = true
  Tip = -> Fillet011
  TreeRank = 0
  ValidateShape = true
  _ExportChildren = -> [Pad020,Fillet008,Fillet009,Fillet010,Pocket012,PolarPattern013,Fillet011]
  _GroupVersion = 1
COMPONENT P3 — recipe-attached ("Poignee", modeled in this document).
Construction recipe (the document's own serialized feature program — sketch geometry with constraints, then the solid features built on it; lengths are millimeters unless a unit is written):

FEATURE [Part::Part2DObjectPython] ShapeString  # Draft 2D object (typed FeaturePython)
  FontFile = <userpath>/Downloads/baveuse/baveuse.ttf
  InvalidShape = false
  Placement = pos=(-35.5,-8,-3) rot=(1,0,0;1.5708rad)
  Size = 5
  String = KARIBOUS
  Tracking = 0
  TreeRank = 0
  ValidateShape = true
FEATURE [Sketcher::SketchObject] Sketch
  ArcFitTolerance = 0
  AttachmentSupport = -> [XZ_Plane]
  ExternalBSplineMaxDegree = 0
  ExternalBSplineTolerance = 0
  FullyConstrained = true
  InternalTolerance = 1e-06
  InvalidShape = false
  MakeInternals = false
  MapMode = 5
  Placement = pos=(0,0,0) rot=(1,0,0;1.5708rad)
  Support = -> [XZ_Plane]
  TreeRank = 0
  ValidateShape = true
  sketch-geometry (4):
    g0: LineSegment StartX=-40 StartY=11 StartZ=0 EndX=40 EndY=11 EndZ=0
    g1: LineSegment StartX=40 StartY=11 StartZ=0 EndX=40 EndY=-7 EndZ=0
    g2: LineSegment StartX=40 StartY=-7 StartZ=0 EndX=-40 EndY=-7 EndZ=0
    g3: LineSegment StartX=-40 StartY=-7 StartZ=0 EndX=-40 EndY=11 EndZ=0
  constraints (11):
    c: Coincident(g0,g1)
    c: Coincident(g1,g2)
    c: Coincident(g2,g3)
    c: Coincident(g3,g0)
    c: Horizontal(g0)
    c: Vertical(g1)
    c: Vertical(g3)
    c: Symmetric(g1,g2,g-2)
    c: DistanceY(g0) = 11
    c: DistanceY(g1,g-1) = 7
    c: DistanceX(g0,g0) = 80
FEATURE [PartDesign::Pad] Pad
  AddSubType = 0
  AutoTaperInnerAngle = false
  CheckUpToFaceLimits = true
  ClaimChildren = false
  Direction = (1,1,1)
  Fit = 0
  FitJoin = 0
  InnerFit = 0
  InnerFitJoin = 0
  InvalidShape = false
  Length = 8
  Length2 = 100
  Linearize = true
  NewSolid = false
  Placement = pos=(0,0,0) rot=(1,0,0;1.5708rad)
  Profile = -> Sketch
  Refine = true
  Suppress = false
  TaperInnerAngle = 0
  TaperInnerAngleRev = 0
  TreeRank = 0
  Type = 0
  ValidateShape = true
  _ProfileBasedVersion = 1
FEATURE [Sketcher::SketchObject] Sketch001
  ArcFitTolerance = 0
  AttachmentSupport = -> [Pad]
  ExternalBSplineMaxDegree = 0
  ExternalBSplineTolerance = 0
  ExternalGeometry = -> [Pad]
  FullyConstrained = true
  InternalTolerance = 1e-06
  InvalidShape = false
  MakeInternals = false
  MapMode = 5
  Placement = pos=(40,0,0) rot=(0.707107,0,0.707107;3.14159rad)
  Support = -> [Pad]
  TreeRank = 0
  ValidateShape = true
  sketch-geometry (4):
    g0: Circle CenterX=-2.5 CenterY=4 CenterZ=0 NormalX=0 NormalY=0 NormalZ=1 AngleXU=0 Radius=2.05
    g1: Circle CenterX=6.5 CenterY=4 CenterZ=0 NormalX=0 NormalY=0 NormalZ=1 AngleXU=0 Radius=2.05
    g2: LineSegment [constr] StartX=-7 StartY=4 StartZ=0 EndX=11 EndY=4 EndZ=0
    g3: LineSegment [constr] StartX=2 StartY=8 StartZ=0 EndX=2 EndY=0 EndZ=0
  constraints (10):
    c: Horizontal(g1,g0)
    c: PointOnObject(g2,g-5)
    c: Horizontal(g2)
    c: PointOnObject(g3,g-1)
    c: Symmetric(g-4,g-4,g2)
    c: Symmetric(g-4,g-5,g3)
    c: Equal(g0,g1)
    c: Symmetric(g0,g1,g3)
    c: Diameter(g1) = 4.1
    c: Symmetric(g-5,g3,g0)
FEATURE [PartDesign::Pocket] Pocket
  AddSubType = 1
  AutoTaperInnerAngle = false
  BaseFeature = -> Pad
  CheckUpToFaceLimits = true
  ClaimChildren = false
  Direction = (1,1,1)
  Fit = 0
  FitJoin = 0
  InnerFit = 0
  InnerFitJoin = 0
  InvalidShape = false
  Length = 12
  Length2 = 100
  Linearize = true
  NewSolid = false
  Placement = pos=(0,0,0) rot=(1,0,0;1.5708rad)
  Profile = -> Sketch001
  Refine = true
  Suppress = false
  TaperInnerAngle = 0
  TaperInnerAngleRev = 0
  TreeRank = 0
  Type = 0
  ValidateShape = true
  _ProfileBasedVersion = 1
  _Version = 1
FEATURE [PartDesign::Mirrored] Mirrored005
  AddSubType = 0
  BaseFeature = -> Pocket
  CopyShape = false
  InvalidShape = false
  MirrorPlane = -> YZ_Plane
  NewSolid = false
  OriginalSubs = -> [Pocket]
  Originals = -> [Pocket]
  ParallelTransform = true
  Placement = pos=(0,0,0) rot=(1,0,0;1.5708rad)
  Refine = true
  SubTransform = true
  Suppress = false
  TreeRank = 0
  ValidateShape = true
  _Version = 3
FEATURE [PartDesign::Chamfer] Chamfer
  AddSubType = 0
  Angle = 45
  Base = -> Mirrored005 [Edge9,Edge8,Edge13,Edge14]
  BaseFeature = -> Mirrored005
  ChamferType = 0
  FlipDirection = false
  InvalidShape = false
  NewSolid = false
  Placement = pos=(0,0,0) rot=(1,0,0;1.5708rad)
  Refine = true
  Size = 0.4
  Size2 = 1
  SupportTransform = false
  Suppress = false
  TreeRank = 0
  UseAllEdges = false
  ValidateShape = true
FEATURE [PartDesign::Chamfer] Chamfer001
  AddSubType = 0
  Angle = 45
  Base = -> Chamfer [Edge11,Edge10,Edge12]
  BaseFeature = -> Chamfer
  ChamferType = 0
  FlipDirection = false
  InvalidShape = false
  NewSolid = false
  Placement = pos=(0,0,0) rot=(1,0,0;1.5708rad)
  Refine = true
  Size = 0.4
  Size2 = 1
  SupportTransform = false
  Suppress = false
  TreeRank = 0
  UseAllEdges = false
  ValidateShape = true
FEATURE [PartDesign::Fillet] Fillet
  AddSubType = 0
  Base = -> Chamfer001 [Edge20]
  BaseFeature = -> Chamfer001
  InvalidShape = false
  NewSolid = false
  Placement = pos=(0,0,0) rot=(1,0,0;1.5708rad)
  Radius = 2
  Refine = true
  SupportTransform = false
  Suppress = false
  TreeRank = 0
  UseAllEdges = false
  ValidateShape = true
FEATURE [PartDesign::Pocket] Pocket001
  AddSubType = 1
  AutoTaperInnerAngle = false
  BaseFeature = -> Fillet
  CheckUpToFaceLimits = true
  ClaimChildren = false
  Direction = (1,1,1)
  Fit = 0
  FitJoin = 0
  InnerFit = 0
  InnerFitJoin = 0
  InvalidShape = false
  Length = 0.5
  Length2 = 100
  Linearize = true
  NewSolid = false
  Placement = pos=(0,0,0) rot=(1,0,0;1.5708rad)
  Profile = -> ShapeString
  Refine = true
  Suppress = false
  TaperInnerAngle = 0
  TaperInnerAngleRev = 0
  TreeRank = 0
  Type = 0
  ValidateShape = true
  _ProfileBasedVersion = 1
  _Version = 1
FEATURE [PartDesign::Body] Body  label="Front"
  AutoGroupSolids = false
  ClaimAllChildren = false
  ExportMode = 0
  Group = -> [Sketch,Pad,Sketch001,Pocket,Mirrored005,Chamfer,Chamfer001,Fillet,ShapeString,Pocket001]
  InvalidShape = false
  Origin = -> Origin
  Placement = pos=(-6.99382e-06,40,0) rot=(0,0,1;3.14159rad)
  SingleSolid = true
  Tip = -> Pocket001
  TreeRank = 0
  ValidateShape = true
  _ExportChildren = -> [Pad,Pocket,Mirrored005,Chamfer,Chamfer001,Fillet,Pocket001]
  _GroupVersion = 1
FEATURE [Sketcher::SketchObject] Sketch058
  ArcFitTolerance = 0
  AttachmentSupport = -> [YZ_Plane034]
  ExternalBSplineMaxDegree = 0
  ExternalBSplineTolerance = 0
  FullyConstrained = true
  InternalTolerance = 1e-06
  InvalidShape = false
  MakeInternals = false
  MapMode = 5
  Placement = pos=(0,0,0) rot=(0.57735,0.57735,0.57735;2.0944rad)
  Support = -> [YZ_Plane034]
  TreeRank = 0
  ValidateShape = true
  sketch-geometry (10):
    g0: LineSegment StartX=-8 StartY=-7 StartZ=0 EndX=-8 EndY=11 EndZ=0
    g1: LineSegment StartX=-8 StartY=11 StartZ=0 EndX=0 EndY=11 EndZ=0
    g2: LineSegment StartX=0 StartY=11 StartZ=0 EndX=47 EndY=7 EndZ=0
    g3: LineSegment StartX=47 StartY=7 StartZ=0 EndX=47 EndY=-7 EndZ=0
    g4: LineSegment StartX=47 StartY=-7 StartZ=0 EndX=-8 EndY=-7 EndZ=0
    g5: Circle CenterX=40 CenterY=0 CenterZ=0 NormalX=0 NormalY=0 NormalZ=1 AngleXU=0 Radius=4
    g6: Circle CenterX=-4 CenterY=6.5 CenterZ=0 NormalX=0 NormalY=0 NormalZ=1 AngleXU=0 Radius=1.6
    g7: Circle CenterX=-4 CenterY=-2.5 CenterZ=0 NormalX=0 NormalY=0 NormalZ=1 AngleXU=0 Radius=1.6
    g8: LineSegment [constr] StartX=-4 StartY=11 StartZ=0 EndX=-4 EndY=-7 EndZ=0
    g9: LineSegment [constr] StartX=-8 StartY=2 StartZ=0 EndX=0 EndY=2 EndZ=0
  constraints (27):
    c: Vertical(g0)
    c: Coincident(g0,g1)
    c: PointOnObject(g1,g-2)
    c: Horizontal(g1)
    c: Coincident(g1,g2)
    c: Coincident(g2,g3)
    c: Coincident(g3,g4)
    c: Coincident(g4,g0)
    c: Horizontal(g4)
    c: DistanceY(g0) = -7
    c: DistanceY(g0) = 11
    c: PointOnObject(g5,g-1)
    c: DistanceX(g5) = 40
    c: Symmetric(g2,g3,g-1)
    c: Diameter(g5) = 8
    c: DistanceX(g2) = 47
    c: DistanceX(g1,g1) = 8
    c: Vertical(g7,g6)
    c: PointOnObject(g8,g4)
    c: Vertical(g8)
    c: PointOnObject(g9,g-2)
    c: Symmetric(g0,g0,g9)
    c: Symmetric(g0,g1,g8)
    c: Symmetric(g6,g7,g9)
    c: Diameter(g6) = 3.2
    c: Equal(g6,g7)
    c: Symmetric(g9,g1,g6)
FEATURE [PartDesign::Pad] Pad032
  AddSubType = 0
  AutoTaperInnerAngle = false
  CheckUpToFaceLimits = true
  ClaimChildren = false
  Direction = (1,1,1)
  Fit = 0
  FitJoin = 0
  InnerFit = 0
  InnerFitJoin = 0
  InvalidShape = false
  Length = 3
  Length2 = 100
  Linearize = true
  NewSolid = false
  Placement = pos=(0,0,0) rot=(0.57735,0.57735,0.57735;2.0944rad)
  Profile = -> Sketch058
  Refine = true
  Suppress = false
  TaperInnerAngle = 0
  TaperInnerAngleRev = 0
  TreeRank = 0
  Type = 0
  ValidateShape = true
  _ProfileBasedVersion = 1
FEATURE [PartDesign::Fillet] Fillet017
  AddSubType = 0
  Base = -> Pad032 [Edge2]
  BaseFeature = -> Pad032
  InvalidShape = false
  NewSolid = false
  Placement = pos=(0,0,0) rot=(0.57735,0.57735,0.57735;2.0944rad)
  Radius = 2
  Refine = true
  SupportTransform = false
  Suppress = false
  TreeRank = 0
  UseAllEdges = false
  ValidateShape = true
FEATURE [PartDesign::Fillet] Fillet020
  AddSubType = 0
  Base = -> Fillet017 [Edge24,Edge15]
  BaseFeature = -> Fillet017
  InvalidShape = false
  NewSolid = false
  Placement = pos=(0,0,0) rot=(0.57735,0.57735,0.57735;2.0944rad)
  Radius = 7.1
  Refine = true
  SupportTransform = false
  Suppress = false
  TreeRank = 0
  UseAllEdges = false
  ValidateShape = true
FEATURE [PartDesign::Chamfer] Chamfer016
  AddSubType = 0
  Angle = 45
  Base = -> Fillet020 [Edge13]
  BaseFeature = -> Fillet020
  ChamferType = 0
  FlipDirection = false
  InvalidShape = false
  NewSolid = false
  Placement = pos=(0,0,0) rot=(0.57735,0.57735,0.57735;2.0944rad)
  Refine = true
  Size = 0.4
  Size2 = 1
  SupportTransform = false
  Suppress = false
  TreeRank = 0
  UseAllEdges = false
  ValidateShape = true
FEATURE [PartDesign::Body] Body027  label="Lateral"
  AutoGroupSolids = false
  ClaimAllChildren = false
  ExportMode = 0
  Group = -> [Sketch058,Pad032,Fillet017,Fillet020,Chamfer016]
  InvalidShape = false
  Origin = -> Origin044
  Placement = pos=(-40,40,0) rot=(0,0,1;3.14159rad)
  SingleSolid = true
  Tip = -> Chamfer016
  TreeRank = 0
  ValidateShape = true
  _ExportChildren = -> [Pad032,Fillet017,Fillet020,Chamfer016]
  _GroupVersion = 1
FEATURE [Sketcher::SketchObject] Sketch059
  ArcFitTolerance = 0
  AttachmentSupport = -> [YZ_Plane035]
  ExternalBSplineMaxDegree = 0
  ExternalBSplineTolerance = 0
  FullyConstrained = true
  InternalTolerance = 1e-06
  InvalidShape = false
  MakeInternals = false
  MapMode = 5
  Placement = pos=(0,0,0) rot=(0.57735,0.57735,0.57735;2.0944rad)
  Support = -> [YZ_Plane035]
  TreeRank = 0
  ValidateShape = true
  sketch-geometry (10):
    g0: LineSegment StartX=-8 StartY=-7 StartZ=0 EndX=-8 EndY=11 EndZ=0
    g1: LineSegment StartX=-8 StartY=11 StartZ=0 EndX=0 EndY=11 EndZ=0
    g2: LineSegment StartX=0 StartY=11 StartZ=0 EndX=47 EndY=7 EndZ=0
    g3: LineSegment StartX=47 StartY=7 StartZ=0 EndX=47 EndY=-7 EndZ=0
    g4: LineSegment StartX=47 StartY=-7 StartZ=0 EndX=-8 EndY=-7 EndZ=0
    g5: Circle CenterX=40 CenterY=0 CenterZ=0 NormalX=0 NormalY=0 NormalZ=1 AngleXU=0 Radius=1.7
    g6: Circle CenterX=-4 CenterY=6.5 CenterZ=0 NormalX=0 NormalY=0 NormalZ=1 AngleXU=0 Radius=1.6
    g7: Circle CenterX=-4 CenterY=-2.5 CenterZ=0 NormalX=0 NormalY=0 NormalZ=1 AngleXU=0 Radius=1.6
    g8: LineSegment [constr] StartX=-4 StartY=11 StartZ=0 EndX=-4 EndY=-7 EndZ=0
    g9: LineSegment [constr] StartX=-8 StartY=2 StartZ=0 EndX=0 EndY=2 EndZ=0
  constraints (27):
    c: Vertical(g0)
    c: Coincident(g0,g1)
    c: PointOnObject(g1,g-2)
    c: Horizontal(g1)
    c: Coincident(g1,g2)
    c: Coincident(g2,g3)
    c: Coincident(g3,g4)
    c: Coincident(g4,g0)
    c: Horizontal(g4)
    c: DistanceY(g0) = -7
    c: DistanceY(g0) = 11
    c: PointOnObject(g5,g-1)
    c: DistanceX(g5) = 40
    c: Symmetric(g2,g3,g-1)
    c: Diameter(g5) = 3.4
    c: DistanceX(g2) = 47
    c: DistanceX(g1,g1) = 8
    c: Vertical(g7,g6)
    c: PointOnObject(g8,g4)
    c: Vertical(g8)
    c: PointOnObject(g9,g-2)
    c: Symmetric(g0,g0,g9)
    c: Symmetric(g0,g1,g8)
    c: Symmetric(g6,g7,g9)
    c: Diameter(g6) = 3.2
    c: Equal(g6,g7)
    c: Symmetric(g9,g1,g6)
FEATURE [PartDesign::Pad] Pad033
  AddSubType = 0
  AutoTaperInnerAngle = false
  CheckUpToFaceLimits = true
  ClaimChildren = false
  Direction = (1,1,1)
  Fit = 0
  FitJoin = 0
  InnerFit = 0
  InnerFitJoin = 0
  InvalidShape = false
  Length = 3
  Length2 = 100
  Linearize = true
  NewSolid = false
  Placement = pos=(0,0,0) rot=(0.57735,0.57735,0.57735;2.0944rad)
  Profile = -> Sketch059
  Refine = true
  Suppress = false
  TaperInnerAngle = 0
  TaperInnerAngleRev = 0
  TreeRank = 0
  Type = 0
  ValidateShape = true
  _ProfileBasedVersion = 1
FEATURE [PartDesign::Fillet] Fillet021
  AddSubType = 0
  Base = -> Pad033 [Edge2]
  BaseFeature = -> Pad033
  InvalidShape = false
  NewSolid = false
  Placement = pos=(0,0,0) rot=(0.57735,0.57735,0.57735;2.0944rad)
  Radius = 2
  Refine = true
  SupportTransform = false
  Suppress = false
  TreeRank = 0
  UseAllEdges = false
  ValidateShape = true
FEATURE [PartDesign::Fillet] Fillet022
  AddSubType = 0
  Base = -> Fillet021 [Edge24,Edge15]
  BaseFeature = -> Fillet021
  InvalidShape = false
  NewSolid = false
  Placement = pos=(0,0,0) rot=(0.57735,0.57735,0.57735;2.0944rad)
  Radius = 7.1
  Refine = true
  SupportTransform = false
  Suppress = false
  TreeRank = 0
  UseAllEdges = false
  ValidateShape = true
FEATURE [PartDesign::Chamfer] Chamfer017
  AddSubType = 0
  Angle = 45
  Base = -> Fillet022 [Edge13]
  BaseFeature = -> Fillet022
  ChamferType = 0
  FlipDirection = false
  InvalidShape = false
  NewSolid = false
  Placement = pos=(0,0,0) rot=(0.57735,0.57735,0.57735;2.0944rad)
  Refine = true
  Size = 0.4
  Size2 = 1
  SupportTransform = false
  Suppress = false
  TreeRank = 0
  UseAllEdges = false
  ValidateShape = true
FEATURE [PartDesign::Body] Body028  label="Lateral001"
  AutoGroupSolids = false
  ClaimAllChildren = false
  ExportMode = 0
  Group = -> [Sketch059,Pad033,Fillet021,Fillet022,Chamfer017]
  InvalidShape = false
  Origin = -> Origin045
  Placement = pos=(-43,40,-8.9e-15) rot=(0,0,1;3.14159rad)
  SingleSolid = true
  Tip = -> Chamfer017
  TreeRank = 0
  ValidateShape = true
  _ExportChildren = -> [Pad033,Fillet021,Fillet022,Chamfer017]
  _GroupVersion = 1
COMPONENT P4 — recipe-attached ("SupportGauche3D", modeled in this document).
Construction recipe (the document's own serialized feature program — sketch geometry with constraints, then the solid features built on it; lengths are millimeters unless a unit is written):

FEATURE [Sketcher::SketchObject] Sketch037
  ArcFitTolerance = 0
  AttachmentSupport = -> [XZ_Plane030]
  ExternalBSplineMaxDegree = 0
  ExternalBSplineTolerance = 0
  FullyConstrained = true
  InternalTolerance = 1e-06
  InvalidShape = false
  MakeInternals = false
  MapMode = 5
  Placement = pos=(0,0,0) rot=(1,0,0;1.5708rad)
  Support = -> [XZ_Plane030]
  TreeRank = 0
  ValidateShape = true
  sketch-geometry (6):
    g0: LineSegment StartX=-5 StartY=0 StartZ=0 EndX=15 EndY=0 EndZ=0
    g1: LineSegment StartX=15 StartY=0 StartZ=0 EndX=15 EndY=-7 EndZ=0
    g2: LineSegment StartX=15 StartY=-7 StartZ=0 EndX=5 EndY=-7 EndZ=0
    g3: LineSegment StartX=5 StartY=-7 StartZ=0 EndX=5 EndY=-32 EndZ=0
    g4: LineSegment StartX=5 StartY=-32 StartZ=0 EndX=-5 EndY=-32 EndZ=0
    g5: LineSegment StartX=-5 StartY=-32 StartZ=0 EndX=-5 EndY=0 EndZ=0
  constraints (18):
    c: PointOnObject(g0,g-1)
    c: Horizontal(g0)
    c: Coincident(g0,g1)
    c: Vertical(g1)
    c: Coincident(g1,g2)
    c: Horizontal(g2)
    c: Coincident(g2,g3)
    c: Vertical(g3)
    c: Coincident(g3,g4)
    c: Horizontal(g4)
    c: Coincident(g4,g5)
    c: Coincident(g5,g0)
    c: Vertical(g5)
    c: DistanceY(g1,g1) = 7
    c: DistanceX(g-1,g2) = 5
    c: DistanceX(g2,g2) = 10
    c: DistanceY(g3,g3) = 25
    c: DistanceX(g0,g-1) = 5
FEATURE [PartDesign::Pad] Pad024
  AddSubType = 0
  AutoTaperInnerAngle = false
  CheckUpToFaceLimits = true
  ClaimChildren = false
  Direction = (1,1,1)
  Fit = 0
  FitJoin = 0
  InnerFit = 0
  InnerFitJoin = 0
  InvalidShape = false
  Length = 10
  Length2 = 100
  Linearize = true
  NewSolid = false
  Placement = pos=(0,0,0) rot=(1,0,0;1.5708rad)
  Profile = -> Sketch037
  Refine = true
  Reversed = true
  Suppress = false
  TaperInnerAngle = 0
  TaperInnerAngleRev = 0
  TreeRank = 0
  Type = 0
  ValidateShape = true
  _ProfileBasedVersion = 1
FEATURE [PartDesign::Pad] Pad025
  AddSubType = 0
  AutoTaperInnerAngle = false
  BaseFeature = -> Pad024
  CheckUpToFaceLimits = true
  ClaimChildren = false
  Direction = (1,1,1)
  Fit = 0
  FitJoin = 0
  InnerFit = 0
  InnerFitJoin = 0
  InvalidShape = false
  Length = 5
  Length2 = 100
  Linearize = true
  NewSolid = false
  Placement = pos=(0,0,0) rot=(1,0,0;1.5708rad)
  Profile = -> Sketch037
  Refine = true
  Suppress = false
  TaperInnerAngle = 0
  TaperInnerAngleRev = 0
  TreeRank = 0
  Type = 0
  ValidateShape = true
  _ProfileBasedVersion = 1
FEATURE [Sketcher::SketchObject] Sketch038
  ArcFitTolerance = 0
  AttachmentSupport = -> [XZ_Plane030]
  ExternalBSplineMaxDegree = 0
  ExternalBSplineTolerance = 0
  ExternalGeometry = -> [Pad025]
  FullyConstrained = true
  InternalTolerance = 1e-06
  InvalidShape = false
  MakeInternals = false
  MapMode = 5
  Placement = pos=(0,0,0) rot=(1,0,0;1.5708rad)
  Support = -> [XZ_Plane030]
  TreeRank = 0
  ValidateShape = true
  sketch-geometry (4):
    g0: LineSegment StartX=0 StartY=0 StartZ=0 EndX=-5 EndY=0 EndZ=0
    g1: LineSegment StartX=-5 StartY=0 StartZ=0 EndX=-5 EndY=-32 EndZ=0
    g2: LineSegment StartX=-5 StartY=-32 StartZ=0 EndX=0 EndY=-32 EndZ=0
    g3: LineSegment StartX=0 StartY=-32 StartZ=0 EndX=0 EndY=0 EndZ=0
  constraints (10):
    c: Coincident(g0,g1)
    c: Coincident(g1,g2)
    c: Coincident(g2,g3)
    c: Coincident(g3,g0)
    c: Horizontal(g0)
    c: Horizontal(g2)
    c: Vertical(g1)
    c: Vertical(g3)
    c: Coincident(g0,g-1)
    c: Coincident(g-3,g1)
FEATURE [PartDesign::Pocket] Pocket013
  AddSubType = 1
  AutoTaperInnerAngle = false
  BaseFeature = -> Pad025
  CheckUpToFaceLimits = true
  ClaimChildren = false
  Direction = (1,1,1)
  Fit = 0
  FitJoin = 0
  InnerFit = 0
  InnerFitJoin = 0
  InvalidShape = false
  Length = 5
  Length2 = 100
  Linearize = true
  NewSolid = false
  Placement = pos=(0,0,0) rot=(1,0,0;1.5708rad)
  Profile = -> Sketch038
  Refine = true
  Suppress = false
  TaperInnerAngle = 0
  TaperInnerAngleRev = 0
  TreeRank = 0
  Type = 1
  ValidateShape = true
  _ProfileBasedVersion = 1
  _Version = 0
FEATURE [Sketcher::SketchObject] Sketch039
  ArcFitTolerance = 0
  AttachmentSupport = -> [Pocket013]
  ExternalBSplineMaxDegree = 0
  ExternalBSplineTolerance = 0
  ExternalGeometry = -> [Pocket013]
  FullyConstrained = true
  InternalTolerance = 1e-06
  InvalidShape = false
  MakeInternals = false
  MapMode = 5
  Placement = pos=(0,-5,-1.1e-15) rot=(1,0,0;1.5708rad)
  Support = -> [Pocket013]
  TreeRank = 0
  ValidateShape = true
  sketch-geometry (3):
    g0: LineSegment StartX=15 StartY=-7 StartZ=0 EndX=5 EndY=-19.5 EndZ=0
    g1: LineSegment StartX=5 StartY=-7 StartZ=0 EndX=5 EndY=-19.5 EndZ=0
    g2: LineSegment StartX=5 StartY=-7 StartZ=0 EndX=15 EndY=-7 EndZ=0
  constraints (6):
    c: Coincident(g0,g-3)
    c: Coincident(g1,g-4)
    c: Coincident(g1,g0)
    c: Coincident(g2,g1)
    c: Coincident(g2,g0)
    c: Symmetric(g1,g-4,g0)
FEATURE [PartDesign::Pad] Pad026
  AddSubType = 0
  AutoTaperInnerAngle = false
  BaseFeature = -> Pocket013
  CheckUpToFaceLimits = true
  ClaimChildren = false
  Direction = (1,1,1)
  Fit = 0
  FitJoin = 0
  InnerFit = 0
  InnerFitJoin = 0
  InvalidShape = false
  Length = 2
  Length2 = 100
  Linearize = true
  NewSolid = false
  Placement = pos=(0,0,0) rot=(1,0,0;1.5708rad)
  Profile = -> Sketch039
  Refine = true
  Reversed = true
  Suppress = false
  TaperInnerAngle = 0
  TaperInnerAngleRev = 0
  TreeRank = 0
  Type = 0
  ValidateShape = true
  _ProfileBasedVersion = 1
FEATURE [Sketcher::SketchObject] Sketch040
  ArcFitTolerance = 0
  AttachmentSupport = -> [XY_Plane030]
  ExternalBSplineMaxDegree = 0
  ExternalBSplineTolerance = 0
  ExternalGeometry = -> [Pad026]
  FullyConstrained = true
  InternalTolerance = 1e-06
  InvalidShape = false
  MakeInternals = false
  MapMode = 5
  Support = -> [XY_Plane030]
  TreeRank = 0
  ValidateShape = true
  sketch-geometry (1):
    g0: Circle CenterX=10 CenterY=5 CenterZ=0 NormalX=0 NormalY=0 NormalZ=1 AngleXU=0 Radius=2.05
  constraints (3):
    c: DistanceX(g0,g-3) = 5
    c: DistanceY(g0,g-3) = 5
    c: Diameter(g0) = 4.1
FEATURE [PartDesign::Pocket] Pocket014
  AddSubType = 1
  AutoTaperInnerAngle = false
  BaseFeature = -> Pad026
  CheckUpToFaceLimits = true
  ClaimChildren = false
  Direction = (1,1,1)
  Fit = 0
  FitJoin = 0
  InnerFit = 0
  InnerFitJoin = 0
  InvalidShape = false
  Length = 5
  Length2 = 100
  Linearize = true
  NewSolid = false
  Placement = pos=(0,0,0) rot=(1,0,0;1.5708rad)
  Profile = -> Sketch040
  Refine = true
  Suppress = false
  TaperInnerAngle = 0
  TaperInnerAngleRev = 0
  TreeRank = 0
  Type = 1
  ValidateShape = true
  _ProfileBasedVersion = 1
  _Version = 0
FEATURE [Sketcher::SketchObject] Sketch041
  ArcFitTolerance = 0
  AttachmentSupport = -> [Pocket014]
  ExternalBSplineMaxDegree = 0
  ExternalBSplineTolerance = 0
  ExternalGeometry = -> [Pocket014]
  FullyConstrained = true
  InternalTolerance = 1e-06
  InvalidShape = false
  MakeInternals = false
  MapMode = 5
  Placement = pos=(5,0,0) rot=(0.707107,0,0.707107;3.14159rad)
  Support = -> [Pocket014]
  TreeRank = 0
  ValidateShape = true
  sketch-geometry (4):
    g0: Circle CenterX=-27 CenterY=-5 CenterZ=0 NormalX=0 NormalY=0 NormalZ=1 AngleXU=0 Radius=1.6
    g1: Circle CenterX=-12 CenterY=-5 CenterZ=0 NormalX=0 NormalY=0 NormalZ=1 AngleXU=0 Radius=1.6
    g2: LineSegment [constr] StartX=-32 StartY=-5 StartZ=0 EndX=-7 EndY=-5 EndZ=0
    g3: GeomPoint [constr] X=-19.5 Y=-5 Z=0
  constraints (10):
    c: Diameter(g0) = 3.2
    c: Equal(g0,g1)
    c: Horizontal(g1,g0)
    c: PointOnObject(g2,g-4)
    c: PointOnObject(g2,g-3)
    c: Horizontal(g2)
    c: DistanceY(g-5,g2) = 5
    c: Symmetric(g2,g2,g3)
    c: Symmetric(g0,g1,g3)
    c: DistanceX(g2,g0) = 5
FEATURE [PartDesign::Pocket] Pocket015
  AddSubType = 1
  AutoTaperInnerAngle = false
  BaseFeature = -> Pocket014
  CheckUpToFaceLimits = true
  ClaimChildren = false
  Direction = (1,1,1)
  Fit = 0
  FitJoin = 0
  InnerFit = 0
  InnerFitJoin = 0
  InvalidShape = false
  Length = 5
  Length2 = 100
  Linearize = true
  NewSolid = false
  Placement = pos=(0,0,0) rot=(1,0,0;1.5708rad)
  Profile = -> Sketch041
  Refine = true
  Suppress = false
  TaperInnerAngle = 0
  TaperInnerAngleRev = 0
  TreeRank = 0
  Type = 1
  ValidateShape = true
  _ProfileBasedVersion = 1
  _Version = 0
FEATURE [Sketcher::SketchObject] Sketch042
  ArcFitTolerance = 0
  AttachmentSupport = -> [Pocket015]
  ExternalBSplineMaxDegree = 0
  ExternalBSplineTolerance = 0
  ExternalGeometry = -> [Pocket015]
  FullyConstrained = true
  InternalTolerance = 1e-06
  InvalidShape = false
  MakeInternals = false
  MapMode = 5
  Placement = pos=(5,0,0) rot=(0.707107,0,0.707107;3.14159rad)
  Support = -> [Pocket015]
  TreeRank = 0
  ValidateShape = true
  sketch-geometry (5):
    g0: LineSegment StartX=-32 StartY=-10 StartZ=0 EndX=-32 EndY=-0.75 EndZ=0
    g1: LineSegment StartX=-32 StartY=-10 StartZ=0 EndX=-7.75 EndY=-10 EndZ=0
    g2: LineSegment StartX=-7.75 StartY=-10 StartZ=0 EndX=-7.75 EndY=-5 EndZ=0
    g3: ArcOfCircle CenterX=-12 CenterY=-5 CenterZ=0 NormalX=0 NormalY=0 NormalZ=1 AngleXU=0 Radius=4.25 StartAngle=0 EndAngle=1.5708
    g4: LineSegment StartX=-32 StartY=-0.75 StartZ=0 EndX=-12 EndY=-0.75 EndZ=0
  constraints (12):
    c: Coincident(g0,g-4)
    c: PointOnObject(g0,g-3)
    c: Coincident(g1,g0)
    c: PointOnObject(g1,g-4)
    c: Coincident(g2,g1)
    c: Vertical(g2)
    c: Coincident(g4,g0)
    c: Horizontal(g4)
    c: Tangent(g4,g3) = 1.5708
    c: Tangent(g3,g2) = -1.5708
    c: Coincident(g3,g-5)
    c: Diameter(g3) = 8.5
FEATURE [PartDesign::Pocket] Pocket016
  AddSubType = 1
  AutoTaperInnerAngle = false
  BaseFeature = -> Pocket015
  CheckUpToFaceLimits = true
  ClaimChildren = false
  Direction = (1,1,1)
  Fit = 0
  FitJoin = 0
  InnerFit = 0
  InnerFitJoin = 0
  InvalidShape = false
  Length = 2.5
  Length2 = 100
  Linearize = true
  NewSolid = false
  Placement = pos=(0,0,0) rot=(1,0,0;1.5708rad)
  Profile = -> Sketch042
  Refine = true
  Suppress = false
  TaperInnerAngle = 0
  TaperInnerAngleRev = 0
  TreeRank = 0
  Type = 0
  ValidateShape = true
  _ProfileBasedVersion = 1
  _Version = 0
FEATURE [PartDesign::Chamfer] Chamfer006
  AddSubType = 0
  Angle = 45
  Base = -> Pocket016 [Edge46,Edge41,Edge42,Edge39,Edge40,Edge36]
  BaseFeature = -> Pocket016
  ChamferType = 0
  FlipDirection = false
  InvalidShape = false
  NewSolid = false
  Placement = pos=(0,0,0) rot=(1,0,0;1.5708rad)
  Refine = true
  Size = 0.2
  Size2 = 1
  SupportTransform = false
  Suppress = false
  TreeRank = 0
  UseAllEdges = false
  ValidateShape = true
FEATURE [PartDesign::Chamfer] Chamfer005
  AddSubType = 0
  Angle = 45
  Base = -> Chamfer006 [Edge9,Edge36,Edge45,Edge21,Edge13]
  BaseFeature = -> Chamfer006
  ChamferType = 0
  FlipDirection = false
  InvalidShape = false
  NewSolid = false
  Placement = pos=(0,0,0) rot=(1,0,0;1.5708rad)
  Refine = true
  Size = 1
  Size2 = 1
  SupportTransform = false
  Suppress = false
  TreeRank = 0
  UseAllEdges = false
  ValidateShape = true
FEATURE [PartDesign::Body] Body023  label="BodySupport3DInter"
  AutoGroupSolids = false
  ClaimAllChildren = false
  ExportMode = 0
  Group = -> [Sketch037,Pad024,Pad025,Sketch038,Pocket013,Sketch039,Pad026,Sketch040,Pocket014,Sketch041,Pocket015,Sketch042,Pocket016,Chamfer006,Chamfer005]
  InvalidShape = false
  Origin = -> Origin034
  SingleSolid = true
  Tip = -> Chamfer005
  TreeRank = 0
  ValidateShape = true
  _ExportChildren = -> [Pad024,Pad025,Pocket013,Pad026,Pocket014,Pocket015,Pocket016,Chamfer006,Chamfer005]
  _GroupVersion = 1
COMPONENT P5 — geometry summary ("SupportDroit3D"; no construction recipe available for this part):
  bounding box: 32.0 x 20.0 x 15.0 mm
  tessellated surface: 3,182 triangles
  volume: 3677 mm^3 (38% of its bounding box)
COMPONENT P6 — recipe-attached ("PartSideModule", modeled in this document).
Construction recipe (the document's own serialized feature program — sketch geometry with constraints, then the solid features built on it; lengths are millimeters unless a unit is written):

FEATURE [Sketcher::SketchObject] Sketch045
  ArcFitTolerance = 0
  AttachmentSupport = -> [XY_Plane032]
  ExternalBSplineMaxDegree = 0
  ExternalBSplineTolerance = 0
  FullyConstrained = true
  InternalTolerance = 1e-06
  InvalidShape = false
  MakeInternals = false
  MapMode = 5
  Support = -> [XY_Plane032]
  TreeRank = 0
  ValidateShape = true
  sketch-geometry (6):
    g0: LineSegment StartX=40 StartY=50 StartZ=0 EndX=40 EndY=40 EndZ=0
    g1: LineSegment StartX=40 StartY=40 StartZ=0 EndX=47.3205 EndY=27.3205 EndZ=0
    g2: LineSegment [constr] StartX=0 StartY=0 StartZ=0 EndX=54.6506 EndY=31.5526 EndZ=0
    g3: LineSegment StartX=40 StartY=50 StartZ=0 EndX=44 EndY=50 EndZ=0
    g4: LineSegment StartX=44 StartY=50 StartZ=0 EndX=54.6506 EndY=31.5526 EndZ=0
    g5: LineSegment StartX=54.6506 StartY=31.5526 StartZ=0 EndX=47.3205 EndY=27.3205 EndZ=0
  constraints (17):
    c: Vertical(g0)
    c: Coincident(g1,g0)
    c: Coincident(g2,g-1)
    c: Angle(g2,g-2) = 1.0472
    c: PointOnObject(g1,g2)
    c: Coincident(g0,g3)
    c: Horizontal(g3)
    c: Coincident(g3,g4)
    c: Coincident(g4,g5)
    c: Coincident(g5,g1)
    c: Parallel(g1,g4)
    c: DistanceX(g2,g0) = 40
    c: DistanceY(g0,g0) = 10
    c: DistanceY(g0) = 40
    c: Perpendicular(g5,g1)
    c: DistanceX(g3,g3) = 4
    c: Coincident(g2,g4)
FEATURE [PartDesign::Plane] DatumPlane004
  AttachmentOffset = pos=(0,0,0) rot=(0,-1,0;1.0472rad)
  AttachmentSupport = -> [YZ_Plane032]
  InvalidShape = false
  Length = 81.5526
  MapMode = 5
  MinimumLength = 10
  MinimumWidth = 10
  Placement = pos=(0,0,0) rot=(0.935113,0.250563,0.250563;1.63783rad)
  ResizeMode = 0
  Support = -> [YZ_Plane032]
  TreeRank = 0
  ValidateShape = true
  Width = 30
FEATURE [PartDesign::Pad] Pad028
  AddSubType = 0
  AutoTaperInnerAngle = false
  CheckUpToFaceLimits = true
  ClaimChildren = false
  Direction = (1,1,1)
  Fit = 0
  FitJoin = 0
  InnerFit = 0
  InnerFitJoin = 0
  InvalidShape = false
  Length = 30
  Length2 = 100
  Linearize = true
  Midplane = true
  NewSolid = false
  Profile = -> Sketch045
  Refine = true
  Suppress = false
  TaperInnerAngle = 0
  TaperInnerAngleRev = 0
  TreeRank = 0
  Type = 0
  ValidateShape = true
  _ProfileBasedVersion = 1
FEATURE [PartDesign::Mirrored] Mirrored
  AddSubType = 0
  BaseFeature = -> Pad028
  CopyShape = false
  InvalidShape = false
  MirrorPlane = -> DatumPlane004
  NewSolid = false
  OriginalSubs = -> [Pad028]
  Originals = -> [Pad028]
  ParallelTransform = true
  Refine = true
  SubTransform = true
  Suppress = false
  TreeRank = 0
  ValidateShape = true
  _Version = 2
FEATURE [Sketcher::SketchObject] Sketch046
  ArcFitTolerance = 0
  AttachmentOffset = pos=(0,0,-10) rot=(0,0,1;0rad)
  AttachmentSupport = -> [Mirrored]
  ExternalBSplineMaxDegree = 0
  ExternalBSplineTolerance = 0
  ExternalGeometry = -> [Mirrored]
  FullyConstrained = true
  InternalTolerance = 1e-06
  InvalidShape = false
  MakeInternals = false
  MapMode = 5
  Placement = pos=(50,0,0) rot=(0.57735,-0.57735,-0.57735;2.0944rad)
  Support = -> [Mirrored]
  TreeRank = 0
  ValidateShape = true
  sketch-geometry (2):
    g0: Circle CenterX=-45 CenterY=10 CenterZ=0 NormalX=0 NormalY=0 NormalZ=1 AngleXU=0 Radius=1.5
    g1: LineSegment [constr] StartX=-45 StartY=15 StartZ=0 EndX=-45 EndY=-15 EndZ=0
  constraints (6):
    c: Diameter(g0) = 3
    c: DistanceY(g0) = 10
    c: PointOnObject(g1,g-4)
    c: Vertical(g1)
    c: Symmetric(g-3,g-3,g1)
    c: PointOnObject(g0,g1)
FEATURE [PartDesign::Hole] Hole
  AddSubType = 1
  BaseFeature = -> Mirrored
  ClaimChildren = false
  CustomThreadClearance = 0
  Depth = 25
  DepthType = 0
  Diameter = 3.2
  DrillForDepth = false
  DrillPoint = 1
  DrillPointAngle = 118
  Fit = 0
  FitJoin = 0
  HoleCutCountersinkAngle = 90
  HoleCutCustomValues = false
  HoleCutDepth = 7.5
  HoleCutDiameter = 8.5
  HoleCutType = 1
  InnerFit = 0
  InnerFitJoin = 0
  InvalidShape = false
  ModelThread = false
  NewSolid = false
  Profile = -> Sketch046
  Refine = true
  Reversed = true
  Suppress = false
  Tapered = false
  TaperedAngle = 90
  ThreadClass = 0
  ThreadDepth = 23.5
  ThreadDepthType = 0
  ThreadDirection = 0
  ThreadFit = 0
  ThreadSize = 0
  ThreadType = 0
  Threaded = false
  TreeRank = 0
  UseCustomThreadClearance = false
  ValidateShape = true
  _ProfileBasedVersion = 1
FEATURE [PartDesign::Mirrored] Mirrored001
  AddSubType = 0
  CopyShape = false
  InvalidShape = false
  MirrorPlane = -> XY_Plane032
  NewSolid = false
  ParallelTransform = true
  Refine = true
  SubTransform = true
  Suppress = false
  TreeRank = 0
  ValidateShape = true
  _Version = 2
FEATURE [PartDesign::Mirrored] Mirrored002
  AddSubType = 0
  CopyShape = false
  InvalidShape = false
  MirrorPlane = -> DatumPlane004
  NewSolid = false
  ParallelTransform = true
  Refine = true
  SubTransform = true
  Suppress = false
  TreeRank = 0
  ValidateShape = true
  _Version = 2
FEATURE [PartDesign::MultiTransform] MultiTransform002
  AddSubType = 0
  BaseFeature = -> Hole
  CopyShape = false
  InvalidShape = false
  NewSolid = false
  OriginalSubs = -> [Hole]
  Originals = -> [Hole]
  ParallelTransform = true
  Refine = true
  SubTransform = true
  Suppress = false
  Transformations = -> [Mirrored001,Mirrored002]
  TreeRank = 0
  ValidateShape = true
  _Version = 2
FEATURE [Sketcher::SketchObject] Sketch047
  ArcFitTolerance = 0
  AttachmentSupport = -> [MultiTransform002]
  ExternalBSplineMaxDegree = 0
  ExternalBSplineTolerance = 0
  FullyConstrained = true
  InternalTolerance = 1e-06
  InvalidShape = false
  MakeInternals = false
  MapMode = 5
  Placement = pos=(54.6506,31.5526,-6.3e-15) rot=(0.377964,0.654654,0.654654;2.41886rad)
  Support = -> [MultiTransform002]
  TreeRank = 0
  ValidateShape = true
  sketch-geometry (1):
    g0: Circle CenterX=7.5 CenterY=10 CenterZ=0 NormalX=0 NormalY=0 NormalZ=1 AngleXU=0 Radius=2.05
  constraints (3):
    c: Diameter(g0) = 4.1
    c: DistanceY(g-1,g0) = 10
    c: DistanceX(g-1,g0) = 7.5
FEATURE [PartDesign::Pocket] Pocket018
  AddSubType = 1
  AutoTaperInnerAngle = false
  BaseFeature = -> MultiTransform002
  CheckUpToFaceLimits = true
  ClaimChildren = false
  Direction = (1,1,1)
  Fit = 0
  FitJoin = 0
  InnerFit = 0
  InnerFitJoin = 0
  InvalidShape = false
  Length = 5
  Length2 = 100
  Linearize = true
  NewSolid = false
  Profile = -> Sketch047
  Refine = true
  Suppress = false
  TaperInnerAngle = 0
  TaperInnerAngleRev = 0
  TreeRank = 0
  Type = 1
  ValidateShape = true
  _ProfileBasedVersion = 1
  _Version = 0
FEATURE [PartDesign::Mirrored] Mirrored003
  AddSubType = 0
  CopyShape = false
  InvalidShape = false
  MirrorPlane = -> DatumPlane004
  NewSolid = false
  ParallelTransform = true
  Refine = true
  SubTransform = true
  Suppress = false
  TreeRank = 0
  ValidateShape = true
  _Version = 2
FEATURE [PartDesign::Mirrored] Mirrored004
  AddSubType = 0
  CopyShape = false
  InvalidShape = false
  MirrorPlane = -> XY_Plane032
  NewSolid = false
  ParallelTransform = true
  Refine = true
  SubTransform = true
  Suppress = false
  TreeRank = 0
  ValidateShape = true
  _Version = 2
FEATURE [PartDesign::MultiTransform] MultiTransform003
  AddSubType = 0
  BaseFeature = -> Pocket018
  CopyShape = false
  InvalidShape = false
  NewSolid = false
  OriginalSubs = -> [Pocket018]
  Originals = -> [Pocket018]
  ParallelTransform = true
  Refine = true
  SubTransform = true
  Suppress = false
  Transformations = -> [Mirrored003,Mirrored004]
  TreeRank = 0
  ValidateShape = true
  _Version = 2
FEATURE [PartDesign::Chamfer] Chamfer008
  AddSubType = 0
  Angle = 45
  Base = -> MultiTransform003 [Edge5,Edge6,Edge38,Edge37,Edge21,Edge19,Edge20,Edge22,Edge30,Edge29,Edge33,Edge34,Edge32,Edge28,Edge35,Edge31]
  BaseFeature = -> MultiTransform003
  ChamferType = 0
  FlipDirection = false
  InvalidShape = false
  NewSolid = false
  Refine = true
  Size = 0.2
  Size2 = 1
  SupportTransform = false
  Suppress = false
  TreeRank = 0
  UseAllEdges = false
  ValidateShape = true
FEATURE [Sketcher::SketchObject] Sketch048
  ArcFitTolerance = 0
  AttachmentSupport = -> [Chamfer008]
  ExternalBSplineMaxDegree = 0
  ExternalBSplineTolerance = 0
  FullyConstrained = true
  InternalTolerance = 1e-06
  InvalidShape = false
  MakeInternals = false
  MapMode = 5
  Placement = pos=(54.6506,31.5526,-6.3e-15) rot=(0.377964,0.654654,0.654654;2.41886rad)
  Support = -> [Chamfer008]
  TreeRank = 0
  ValidateShape = true
  sketch-geometry (16):
    g0: ArcOfCircle CenterX=-15 CenterY=0 CenterZ=0 NormalX=0 NormalY=0 NormalZ=1 AngleXU=0 Radius=1 StartAngle=1.5708 EndAngle=4.71239
    g1: ArcOfCircle CenterX=15 CenterY=0 CenterZ=0 NormalX=0 NormalY=0 NormalZ=1 AngleXU=0 Radius=1 StartAngle=4.71239 EndAngle=7.85398
    g2: LineSegment [constr] StartX=-15 StartY=-1 StartZ=0 EndX=15 EndY=-1 EndZ=0
    g3: LineSegment [constr] StartX=-15 StartY=1 StartZ=0 EndX=15 EndY=1 EndZ=0
    g4: ArcOfCircle CenterX=2.81924e-11 CenterY=-10 CenterZ=0 NormalX=0 NormalY=0 NormalZ=1 AngleXU=0 Radius=1 StartAngle=3.14159 EndAngle=6.28319
    g5: ArcOfCircle CenterX=-2.81924e-11 CenterY=10 CenterZ=0 NormalX=0 NormalY=0 NormalZ=1 AngleXU=0 Radius=1 StartAngle=0 EndAngle=3.14159
    g6: LineSegment [constr] StartX=1 StartY=-10 StartZ=0 EndX=1 EndY=10 EndZ=0
    g7: LineSegment [constr] StartX=-1 StartY=-10 StartZ=0 EndX=-1 EndY=10 EndZ=0
    g8: LineSegment StartX=-15 StartY=1 StartZ=0 EndX=-1 EndY=1 EndZ=0
    g9: LineSegment StartX=-1 StartY=1 StartZ=0 EndX=-1 EndY=10 EndZ=0
    g10: LineSegment StartX=1 StartY=10 StartZ=0 EndX=1 EndY=1 EndZ=0
    g11: LineSegment StartX=1 StartY=1 StartZ=0 EndX=15 EndY=1 EndZ=0
    g12: LineSegment StartX=-15 StartY=-1 StartZ=0 EndX=-1 EndY=-1 EndZ=0
    g13: LineSegment StartX=-1 StartY=-1 StartZ=0 EndX=-1 EndY=-10 EndZ=0
    g14: LineSegment StartX=1 StartY=-10 StartZ=0 EndX=1 EndY=-1 EndZ=0
    g15: LineSegment StartX=1 StartY=-1 StartZ=0 EndX=15 EndY=-1 EndZ=0
  constraints (36):
    c: Tangent(g0,g3) = 1.5708
    c: Tangent(g0,g2) = -1.5708
    c: Tangent(g2,g1) = -1.5708
    c: Tangent(g3,g1) = 1.5708
    c: Horizontal(g2)
    c: Equal(g0,g1)
    c: Tangent(g4,g7) = 1.5708
    c: Tangent(g4,g6) = -1.5708
    c: Tangent(g6,g5) = -1.5708
    c: Tangent(g7,g5) = 1.5708
    c: Vertical(g6)
    c: Equal(g4,g5)
    c: Equal(g5,g0)
    c: Symmetric(g0,g1,g-1)
    c: Symmetric(g4,g5,g-1)
    c: Diameter(g0) = 2
    c: DistanceX(g0,g1) = 30
    c: DistanceY(g4,g5) = 20
    c: Tangent(g0,g8) = 1.5708
    c: Coincident(g8,g9)
    c: Coincident(g9,g5)
    c: Vertical(g9)
    c: Tangent(g5,g10) = 1.5708
    c: Coincident(g11,g10)
    c: Coincident(g11,g1)
    c: Horizontal(g11)
    c: Coincident(g12,g0)
    c: PointOnObject(g12,g7)
    c: Horizontal(g12)
    c: Coincident(g13,g12)
    c: Coincident(g13,g4)
    c: Coincident(g14,g4)
    c: PointOnObject(g14,g2)
    c: Vertical(g14)
    c: Coincident(g15,g14)
    c: Coincident(g15,g1)
FEATURE [PartDesign::Pocket] Pocket019
  AddSubType = 1
  AutoTaperInnerAngle = false
  BaseFeature = -> Chamfer008
  CheckUpToFaceLimits = true
  ClaimChildren = false
  Direction = (1,1,1)
  Fit = 0
  FitJoin = 0
  InnerFit = 0
  InnerFitJoin = 0
  InvalidShape = false
  Length = 0.7
  Length2 = 100
  Linearize = true
  NewSolid = false
  Profile = -> Sketch048
  Refine = true
  Suppress = false
  TaperInnerAngle = 0
  TaperInnerAngleRev = 0
  TreeRank = 0
  Type = 0
  ValidateShape = true
  _ProfileBasedVersion = 1
  _Version = 0
FEATURE [PartDesign::Fillet] Fillet015
  AddSubType = 0
  Base = -> Pocket019 [Edge97,Edge79,Edge85,Edge91]
  BaseFeature = -> Pocket019
  InvalidShape = false
  NewSolid = false
  Radius = 0.5
  Refine = true
  SupportTransform = false
  Suppress = false
  TreeRank = 0
  UseAllEdges = false
  ValidateShape = true
FEATURE [PartDesign::Body] Body025  label="BodyPartSide"
  AutoGroupSolids = false
  ClaimAllChildren = false
  ExportMode = 0
  Group = -> [Sketch045,DatumPlane004,Pad028,Mirrored,Sketch046,Hole,MultiTransform002,Mirrored001,Mirrored002,Sketch047,Pocket018,MultiTransform003,Chamfer008,Mirrored003,Mirrored004,Sketch048,Pocket019,Fillet015]
  InvalidShape = false
  Origin = -> Origin038
  SingleSolid = true
  Tip = -> Fillet015
  TreeRank = 0
  ValidateShape = true
  _ExportChildren = -> [DatumPlane004,Pad028,Mirrored,Hole,MultiTransform002,Pocket018,MultiTransform003,Chamfer008,Pocket019,Fillet015]
  _GroupVersion = 1
COMPONENT P7 — recipe-attached ("EnsembleSemelle", modeled in this document).
Construction recipe (the document's own serialized feature program — sketch geometry with constraints, then the solid features built on it; lengths are millimeters unless a unit is written):

FEATURE [Sketcher::SketchObject] Sketch032
  ArcFitTolerance = 0
  AttachmentSupport = -> [XY_Plane026]
  ExternalBSplineMaxDegree = 0
  ExternalBSplineTolerance = 0
  FullyConstrained = true
  InternalTolerance = 1e-06
  InvalidShape = false
  MakeInternals = false
  MapMode = 5
  Support = -> [XY_Plane026]
  TreeRank = 0
  ValidateShape = true
  sketch-geometry (56):
    g0: LineSegment StartX=-131.619 StartY=-24.0289 StartZ=0 EndX=-58.007 EndY=18.4711 EndZ=0
    g1: LineSegment StartX=-58.007 StartY=18.4711 StartZ=0 EndX=-45 EndY=41 EndZ=0
    g2: LineSegment StartX=-45 StartY=41 StartZ=0 EndX=-45 EndY=126 EndZ=0
    g3: LineSegment StartX=-45 StartY=126 StartZ=0 EndX=45 EndY=126 EndZ=0
    g4: LineSegment StartX=45 StartY=126 StartZ=0 EndX=45 EndY=41 EndZ=0
    g5: LineSegment StartX=45 StartY=41 StartZ=0 EndX=58.007 EndY=18.4711 EndZ=0
    g6: LineSegment StartX=58.007 StartY=18.4711 StartZ=0 EndX=131.619 EndY=-24.0289 EndZ=0
    g7: LineSegment StartX=131.619 StartY=-24.0289 StartZ=0 EndX=86.6192 EndY=-101.971 EndZ=0
    g8: LineSegment StartX=86.6192 StartY=-101.971 StartZ=0 EndX=13.007 EndY=-59.4711 EndZ=0
    g9: LineSegment StartX=13.007 StartY=-59.4711 StartZ=0 EndX=-13.007 EndY=-59.4711 EndZ=0
    g10: LineSegment StartX=-13.007 StartY=-59.4711 StartZ=0 EndX=-86.6192 EndY=-101.971 EndZ=0
    g11: LineSegment StartX=-86.6192 StartY=-101.971 StartZ=0 EndX=-131.619 EndY=-24.0289 EndZ=0
    g12: LineSegment [constr] StartX=-1e-16 StartY=1e-16 StartZ=0 EndX=-1e-16 EndY=126 EndZ=0
    g13: LineSegment [constr] StartX=-1e-16 StartY=1e-16 StartZ=0 EndX=-109.119 EndY=-63 EndZ=0
    g14: LineSegment [constr] StartX=-1e-16 StartY=1e-16 StartZ=0 EndX=109.119 EndY=-63 EndZ=0
    g15: LineSegment StartX=-27.5 StartY=40 StartZ=0 EndX=27.5 EndY=40 EndZ=0
    g16: LineSegment StartX=27.5 StartY=40 StartZ=0 EndX=27.5 EndY=105 EndZ=0
    g17: LineSegment StartX=27.5 StartY=105 StartZ=0 EndX=-27.5 EndY=105 EndZ=0
    g18: LineSegment StartX=-27.5 StartY=105 StartZ=0 EndX=-27.5 EndY=40 EndZ=0
    g19: LineSegment StartX=20.891 StartY=-43.8157 StartZ=0 EndX=48.391 EndY=3.8157 EndZ=0
    g20: LineSegment StartX=48.391 StartY=3.8157 StartZ=0 EndX=104.683 EndY=-28.6843 EndZ=0
    g21: LineSegment StartX=104.683 StartY=-28.6843 StartZ=0 EndX=77.1827 EndY=-76.3157 EndZ=0
    g22: LineSegment StartX=77.1827 StartY=-76.3157 StartZ=0 EndX=20.891 EndY=-43.8157 EndZ=0
    g23: LineSegment StartX=-104.683 StartY=-28.6843 StartZ=0 EndX=-77.1827 EndY=-76.3157 EndZ=0
    g24: LineSegment StartX=-77.1827 StartY=-76.3157 StartZ=0 EndX=-20.891 EndY=-43.8157 EndZ=0
    g25: LineSegment StartX=-20.891 StartY=-43.8157 StartZ=0 EndX=-48.391 EndY=3.8157 EndZ=0
    g26: LineSegment StartX=-48.391 StartY=3.8157 StartZ=0 EndX=-104.683 EndY=-28.6843 EndZ=0
    g27: Circle [constr] CenterX=-1e-16 CenterY=1e-16 CenterZ=0 NormalX=0 NormalY=0 NormalZ=1 AngleXU=0 Radius=48.5412
    g28: LineSegment StartX=-11.547 StartY=-20 StartZ=0 EndX=-23.094 EndY=0 EndZ=0
    g29: LineSegment StartX=-23.094 StartY=-1.3e-15 StartZ=0 EndX=-11.547 EndY=20 EndZ=0
    g30: LineSegment StartX=-11.547 StartY=20 StartZ=0 EndX=11.547 EndY=20 EndZ=0
    g31: LineSegment StartX=11.547 StartY=20 StartZ=0 EndX=23.094 EndY=0 EndZ=0
    g32: LineSegment StartX=23.094 StartY=9e-16 StartZ=0 EndX=11.547 EndY=-20 EndZ=0
    g33: LineSegment StartX=11.547 StartY=-20 StartZ=0 EndX=-11.547 EndY=-20 EndZ=0
    g34: Circle [constr] CenterX=-1e-16 CenterY=1e-16 CenterZ=0 NormalX=0 NormalY=0 NormalZ=1 AngleXU=0 Radius=23.094
    g35: Circle CenterX=-21.6506 CenterY=12.5 CenterZ=0 NormalX=0 NormalY=0 NormalZ=1 AngleXU=0 Radius=1.6
    g36: Circle CenterX=21.6506 CenterY=12.5 CenterZ=0 NormalX=0 NormalY=0 NormalZ=1 AngleXU=0 Radius=1.6
    g37: Circle CenterX=0 CenterY=-25 CenterZ=0 NormalX=0 NormalY=0 NormalZ=1 AngleXU=0 Radius=1.6
    g38: LineSegment [constr] StartX=0 StartY=-25 StartZ=0 EndX=-1e-16 EndY=0 EndZ=0
    g39: LineSegment [constr] StartX=-1e-16 StartY=1e-16 StartZ=0 EndX=21.6506 EndY=12.5 EndZ=0
    g40: LineSegment [constr] StartX=-1e-16 StartY=1e-16 StartZ=0 EndX=-21.6506 EndY=12.5 EndZ=0
    g41: LineSegment [constr] StartX=-45 StartY=126 StartZ=0 EndX=-131.619 EndY=-24.0289 EndZ=0
    g42: LineSegment [constr] StartX=-86.6192 StartY=-101.971 StartZ=0 EndX=86.6192 EndY=-101.971 EndZ=0
    g43: LineSegment [constr] StartX=131.619 StartY=-24.0289 StartZ=0 EndX=45 EndY=126 EndZ=0
    g44: LineSegment [constr] StartX=-45 StartY=126 StartZ=0 EndX=-55 EndY=108.679 EndZ=0
    g45: LineSegment [constr] StartX=-55 StartY=108.679 StartZ=0 EndX=-45 EndY=41 EndZ=0
    g46: LineSegment [constr] StartX=-58.007 StartY=18.4711 StartZ=0 EndX=-121.619 EndY=-6.70835 EndZ=0
    g47: LineSegment [constr] StartX=-121.619 StartY=-6.70835 StartZ=0 EndX=-131.619 EndY=-24.0289 EndZ=0
    g48: LineSegment [constr] StartX=-86.6192 StartY=-101.971 StartZ=0 EndX=-66.6192 EndY=-101.971 EndZ=0
    g49: LineSegment [constr] StartX=-66.6192 StartY=-101.971 StartZ=0 EndX=-13.007 EndY=-59.4711 EndZ=0
    g50: LineSegment [constr] StartX=13.007 StartY=-59.4711 StartZ=0 EndX=66.6192 EndY=-101.971 EndZ=0
    g51: LineSegment [constr] StartX=66.6192 StartY=-101.971 StartZ=0 EndX=86.6192 EndY=-101.971 EndZ=0
    g52: LineSegment [constr] StartX=131.619 StartY=-24.0289 StartZ=0 EndX=121.619 EndY=-6.70835 EndZ=0
    g53: LineSegment [constr] StartX=121.619 StartY=-6.70835 StartZ=0 EndX=58.007 EndY=18.4711 EndZ=0
    g54: LineSegment [constr] StartX=45 StartY=41 StartZ=0 EndX=55 EndY=108.679 EndZ=0
    g55: LineSegment [constr] StartX=55 StartY=108.679 StartZ=0 EndX=45 EndY=126 EndZ=0
  constraints (151):
    c: Coincident(g0,g1)
    c: Coincident(g1,g2)
    c: Vertical(g2)
    c: Coincident(g2,g3)
    c: Horizontal(g3)
    c: Coincident(g3,g4)
    c: Vertical(g4)
    c: Coincident(g4,g5)
    c: Coincident(g5,g6)
    c: Coincident(g6,g7)
    c: Coincident(g7,g8)
    c: Coincident(g8,g9)
    c: Horizontal(g9)
    c: Coincident(g9,g10)
    c: Coincident(g10,g11)
    c: Coincident(g11,g0)
    c: Parallel(g8,g6)
    c: Parallel(g10,g0)
    c: Equal(g4,g6)
    c: Equal(g6,g8)
    c: Equal(g8,g10)
    c: Equal(g10,g0)
    c: Equal(g0,g2)
    c: Perpendicular(g6,g7)
    c: Perpendicular(g11,g10)
    c: Coincident(g12,g-1)
    c: PointOnObject(g12,g3)
    c: Vertical(g12)
    c: Coincident(g13,g12)
    c: Coincident(g14,g12)
    c: Symmetric(g6,g7,g14)
    c: Symmetric(g10,g0,g13)
    c: Perpendicular(g13,g11)
    c: Perpendicular(g7,g14)
    c: DistanceX(g3,g3) = 90
    c: Equal(g9,g5)
    c: Equal(g5,g1)
    c: Angle(g14,g12) = 2.0944
    c: Angle(g12,g13) = 2.0944
    c: DistanceY(g12,g2) = 126
    c: DistanceX(g9,g9) = 26.0141
    c: Coincident(g15,g16)
    c: Coincident(g16,g17)
    c: Coincident(g17,g18)
    c: Coincident(g18,g15)
    c: Horizontal(g15)
    c: Vertical(g16)
    c: Vertical(g18)
    c: Symmetric(g16,g17,g12)
    c: DistanceX(g17,g17) = 55
    c: DistanceY(g16,g16) = 65
    c: Coincident(g19,g20)
    c: Coincident(g20,g21)
    c: Coincident(g21,g22)
    c: Coincident(g22,g19)
    c: Coincident(g23,g24)
    c: Coincident(g24,g25)
    c: Coincident(g25,g26)
    c: Coincident(g26,g23)
    c: Equal(g25,g23)
    c: Equal(g23,g19)
    c: Equal(g19,g21)
    c: Equal(g21,g15)
    c: Equal(g22,g20)
    c: Equal(g20,g16)
    c: Equal(g16,g26)
    c: Equal(g26,g24)
    c: Parallel(g24,g13)
    c: Parallel(g22,g14)
    c: Symmetric(g23,g23,g13)
    c: Symmetric(g21,g20,g14)
    c: Coincident(g27,g12)
    c: PointOnObject(g19,g27)
    c: PointOnObject(g24,g27)
    c: PointOnObject(g15,g27)
    c: Equal(g11,g7)
    c: Equal(g7,g3)
    c: Coincident(g28,g29)
    c: Coincident(g29,g30)
    c: Coincident(g30,g31)
    c: Coincident(g31,g32)
    c: Coincident(g32,g33)
    c: Coincident(g33,g28)
    c: Horizontal(g33)
    c: Horizontal(g30)
    c: Equal(g29,g30)
    c: Equal(g30,g31)
    c: Equal(g31,g32)
    c: Equal(g32,g33)
    c: Equal(g33,g28)
    c: Coincident(g34,g12)
    c: PointOnObject(g30,g34)
    c: PointOnObject(g31,g34)
    c: PointOnObject(g32,g34)
    c: PointOnObject(g28,g34)
    c: PointOnObject(g28,g34)
    c: DistanceY(g12,g30) = 20
    c: PointOnObject(g37,g-2)
    c: Equal(g37,g36)
    c: Equal(g36,g35)
    c: Diameter(g35) = 3.2
    c: Coincident(g38,g37)
    c: Coincident(g38,g12)
    c: Coincident(g39,g12)
    c: Coincident(g39,g36)
    c: Coincident(g40,g12)
    c: Coincident(g40,g35)
    c: Perpendicular(g29,g40)
    c: Perpendicular(g31,g39)
    c: Equal(g40,g38)
    c: Equal(g38,g39)
    c: DistanceY(g38,g38) = 25
    c: Coincident(g41,g3)
    c: Coincident(g41,g11)
    c: Coincident(g42,g11)
    c: Coincident(g42,g7)
    c: Coincident(g43,g7)
    c: Coincident(g43,g3)
    c: Coincident(g3,g44)
    c: PointOnObject(g44,g41)
    c: Coincident(g44,g45)
    c: Coincident(g45,g1)
    c: Coincident(g1,g46)
    c: PointOnObject(g46,g41)
    c: Coincident(g46,g47)
    c: Coincident(g47,g11)
    c: Coincident(g11,g48)
    c: Horizontal(g48)
    c: Coincident(g48,g49)
    c: Coincident(g49,g9)
    c: Coincident(g9,g50)
    c: PointOnObject(g50,g42)
    c: Coincident(g50,g51)
    c: Coincident(g51,g7)
    c: Coincident(g7,g52)
    c: PointOnObject(g52,g43)
    c: Coincident(g52,g53)
    c: Coincident(g53,g5)
    c: Coincident(g5,g54)
    c: PointOnObject(g54,g43)
    c: Coincident(g54,g55)
    c: Coincident(g55,g3)
    c: Equal(g55,g44)
    c: Equal(g44,g47)
    c: Equal(g47,g48)
    c: Equal(g48,g51)
    c: Equal(g55,g52)
    c: DistanceX(g48,g48) = 20
    c: DistanceY(g16) = 105
    c: DistanceY(g50,g12) = 101.971
    c: DistanceY(g4,g4) = 85
FEATURE [PartDesign::Pad] Pad020
  AddSubType = 0
  AutoTaperInnerAngle = false
  CheckUpToFaceLimits = true
  ClaimChildren = false
  Direction = (0,0,1)
  Fit = 0
  FitJoin = 0
  InnerFit = 0
  InnerFitJoin = 0
  InvalidShape = false
  Length = 5
  Length2 = 100
  Linearize = true
  NewSolid = false
  Profile = -> Sketch032
  Refine = true
  Reversed = true
  Suppress = false
  TaperInnerAngle = 0
  TaperInnerAngleRev = 0
  TreeRank = 0
  Type = 0
  ValidateShape = true
  _ProfileBasedVersion = 1
FEATURE [PartDesign::Fillet] Fillet008
  AddSubType = 0
  Base = -> Pad020 [Edge41,Edge44,Edge37,Edge38,Edge65,Edge62,Edge61,Edge68,Edge49,Edge50,Edge53,Edge56]
  BaseFeature = -> Pad020
  InvalidShape = false
  NewSolid = false
  Radius = 3
  Refine = true
  SupportTransform = false
  Suppress = false
  TreeRank = 0
  UseAllEdges = false
  ValidateShape = true
FEATURE [PartDesign::Fillet] Fillet009
  AddSubType = 0
  Base = -> Fillet008 [Edge110,Edge99,Edge107,Edge106,Edge102,Edge103]
  BaseFeature = -> Fillet008
  InvalidShape = false
  NewSolid = false
  Radius = 5
  Refine = true
  SupportTransform = false
  Suppress = false
  TreeRank = 0
  UseAllEdges = false
  ValidateShape = true
FEATURE [PartDesign::Fillet] Fillet010
  AddSubType = 0
  Base = -> Fillet009 [Edge53,Edge57,Edge67,Edge71,Edge77,Edge81]
  BaseFeature = -> Fillet009
  InvalidShape = false
  NewSolid = false
  Radius = 5
  Refine = true
  SupportTransform = false
  Suppress = false
  TreeRank = 0
  UseAllEdges = false
  ValidateShape = true
FEATURE [Sketcher::SketchObject] Sketch033
  ArcFitTolerance = 0
  AttachmentSupport = -> [XY_Plane026]
  ExternalBSplineMaxDegree = 0
  ExternalBSplineTolerance = 0
  FullyConstrained = true
  InternalTolerance = 1e-06
  InvalidShape = false
  MakeInternals = false
  MapMode = 5
  Support = -> [XY_Plane026]
  TreeRank = 0
  ValidateShape = true
  sketch-geometry (13):
    g0: Circle CenterX=-20 CenterY=115 CenterZ=0 NormalX=0 NormalY=0 NormalZ=1 AngleXU=0 Radius=1.75
    g1: Circle CenterX=20 CenterY=115 CenterZ=0 NormalX=0 NormalY=0 NormalZ=1 AngleXU=0 Radius=1.75
    g2: Circle CenterX=-35 CenterY=60 CenterZ=0 NormalX=0 NormalY=0 NormalZ=1 AngleXU=0 Radius=1.75
    g3: Circle CenterX=-35 CenterY=100 CenterZ=0 NormalX=0 NormalY=0 NormalZ=1 AngleXU=0 Radius=1.75
    g4: Circle CenterX=35 CenterY=100 CenterZ=0 NormalX=0 NormalY=0 NormalZ=1 AngleXU=0 Radius=1.75
    g5: Circle CenterX=35 CenterY=60 CenterZ=0 NormalX=0 NormalY=0 NormalZ=1 AngleXU=0 Radius=1.75
    g6: Circle CenterX=-35 CenterY=115 CenterZ=0 NormalX=0 NormalY=0 NormalZ=1 AngleXU=0 Radius=3.1
    g7: Circle CenterX=35 CenterY=115 CenterZ=0 NormalX=0 NormalY=0 NormalZ=1 AngleXU=0 Radius=3.1
    g8: Circle CenterX=-35 CenterY=80 CenterZ=0 NormalX=0 NormalY=0 NormalZ=1 AngleXU=0 Radius=2.2
    g9: Circle CenterX=35 CenterY=80 CenterZ=0 NormalX=0 NormalY=0 NormalZ=1 AngleXU=0 Radius=2.2
    g10: Circle CenterX=-35 CenterY=50 CenterZ=0 NormalX=0 NormalY=0 NormalZ=1 AngleXU=0 Radius=2.2
    g11: Circle CenterX=35 CenterY=50 CenterZ=0 NormalX=0 NormalY=0 NormalZ=1 AngleXU=0 Radius=2.2
    g12: Circle CenterX=-1.0206e-12 CenterY=115 CenterZ=0 NormalX=0 NormalY=0 NormalZ=1 AngleXU=0 Radius=2.2
  constraints (31):
    c: Equal(g0,g3)
    c: Equal(g3,g2)
    c: Equal(g2,g1)
    c: Equal(g1,g4)
    c: Equal(g4,g5)
    c: Diameter(g0) = 3.5
    c: Symmetric(g1,g0,g-2)
    c: Symmetric(g3,g4,g-2)
    c: Symmetric(g2,g5,g-2)
    c: Vertical(g3,g2)
    c: DistanceX(g3,g4) = 70
    c: DistanceX(g0,g1) = 40
    c: DistanceY(g4,g1) = 15
    c: DistanceY(g5,g4) = 40
    c: DistanceY(g-1,g1) = 115
    c: Symmetric(g7,g6,g-2)
    c: Horizontal(g6,g0)
    c: Diameter(g7) = 6.2
    c: Equal(g7,g6)
    c: Vertical(g7,g4)
    c: Equal(g9,g8)
    c: Symmetric(g8,g9,g-2)
    c: Symmetric(g5,g4,g9)
    c: Diameter(g9) = 4.4
    c: Symmetric(g1,g0,g12)
    c: Equal(g12,g11)
    c: Equal(g11,g10)
    c: Equal(g10,g9)
    c: Vertical(g11,g5)
    c: Symmetric(g11,g10,g-2)
    c: DistanceY(g11,g5) = 10
FEATURE [PartDesign::Pocket] Pocket012
  AddSubType = 1
  AutoTaperInnerAngle = false
  BaseFeature = -> Fillet010
  CheckUpToFaceLimits = true
  ClaimChildren = false
  Direction = (1,1,1)
  Fit = 0
  FitJoin = 0
  InnerFit = 0
  InnerFitJoin = 0
  InvalidShape = false
  Length = 5
  Length2 = 100
  Linearize = true
  NewSolid = false
  Profile = -> Sketch033
  Refine = true
  Suppress = false
  TaperInnerAngle = 0
  TaperInnerAngleRev = 0
  TreeRank = 0
  Type = 1
  ValidateShape = true
  _ProfileBasedVersion = 1
  _Version = 0
FEATURE [PartDesign::PolarPattern] PolarPattern013
  AddSubType = 0
  Angle = 360
  Axis = -> Sketch033 [N_Axis]
  BaseFeature = -> Pocket012
  CopyShape = false
  InvalidShape = false
  NewSolid = false
  Occurrences = 3
  OriginalSubs = -> [Pocket012]
  Originals = -> [Pocket012]
  ParallelTransform = true
  Refine = true
  SubTransform = true
  Suppress = false
  TreeRank = 0
  ValidateShape = true
  _Version = 0
FEATURE [PartDesign::Fillet] Fillet011
  AddSubType = 0
  Base = -> PolarPattern013 [Edge190,Edge189,Edge192,Edge196,Edge198,Edge194]
  BaseFeature = -> PolarPattern013
  InvalidShape = false
  NewSolid = false
  Radius = 3
  Refine = true
  SupportTransform = false
  Suppress = false
  TreeRank = 0
  UseAllEdges = false
  ValidateShape = true
FEATURE [PartDesign::Body] Body019  label="Semelle"
  AutoGroupSolids = false
  ClaimAllChildren = false
  ExportMode = 0
  Group = -> [Sketch032,Pad020,Fillet008,Fillet009,Fillet010,Sketch033,Pocket012,PolarPattern013,Fillet011]
  InvalidShape = false
  Origin = -> Origin029
  SingleSolid = true
  Tip = -> Fillet011
  TreeRank = 0
  ValidateShape = true
  _ExportChildren = -> [Pad020,Fillet008,Fillet009,Fillet010,Pocket012,PolarPattern013,Fillet011]
  _GroupVersion = 1
FEATURE [Sketcher::SketchObject] Sketch034
  ArcFitTolerance = 0
  AttachmentSupport = -> [XY_Plane027]
  ExternalBSplineMaxDegree = 0
  ExternalBSplineTolerance = 0
  FullyConstrained = true
  InternalTolerance = 1e-06
  InvalidShape = false
  MakeInternals = false
  MapMode = 5
  Support = -> [XY_Plane027]
  TreeRank = 0
  ValidateShape = true
  sketch-geometry (33):
    g0: LineSegment StartX=-54.641 StartY=14.641 StartZ=0 EndX=-40 EndY=40 EndZ=0
    g1: LineSegment StartX=-40 StartY=40 StartZ=0 EndX=-31 EndY=40 EndZ=0
    g2: LineSegment StartX=-31 StartY=40 StartZ=0 EndX=-31 EndY=34 EndZ=0
    g3: LineSegment StartX=-31 StartY=34 StartZ=0 EndX=31 EndY=34 EndZ=0
    g4: LineSegment StartX=31 StartY=34 StartZ=0 EndX=31 EndY=40 EndZ=0
    g5: LineSegment StartX=31 StartY=40 StartZ=0 EndX=40 EndY=40 EndZ=0
    g6: LineSegment StartX=40 StartY=40 StartZ=0 EndX=54.641 EndY=14.641 EndZ=0
    g7: LineSegment StartX=54.641 StartY=14.641 StartZ=0 EndX=50.141 EndY=6.84679 EndZ=0
    g8: LineSegment StartX=50.141 StartY=6.84679 StartZ=0 EndX=44.9449 EndY=9.84679 EndZ=0
    g9: LineSegment StartX=44.9449 StartY=9.84679 StartZ=0 EndX=13.9449 EndY=-43.8468 EndZ=0
    g10: LineSegment StartX=13.9449 StartY=-43.8468 StartZ=0 EndX=19.141 EndY=-46.8468 EndZ=0
    g11: LineSegment StartX=19.141 StartY=-46.8468 StartZ=0 EndX=14.641 EndY=-54.641 EndZ=0
    g12: LineSegment StartX=14.641 StartY=-54.641 StartZ=0 EndX=-14.641 EndY=-54.641 EndZ=0
    g13: LineSegment StartX=-14.641 StartY=-54.641 StartZ=0 EndX=-19.141 EndY=-46.8468 EndZ=0
    g14: LineSegment StartX=-19.141 StartY=-46.8468 StartZ=0 EndX=-13.9449 EndY=-43.8468 EndZ=0
    g15: LineSegment StartX=-13.9449 StartY=-43.8468 StartZ=0 EndX=-44.9449 EndY=9.84679 EndZ=0
    g16: LineSegment StartX=-44.9449 StartY=9.84679 StartZ=0 EndX=-50.141 EndY=6.84679 EndZ=0
    g17: LineSegment StartX=-50.141 StartY=6.84679 StartZ=0 EndX=-54.641 EndY=14.641 EndZ=0
    g18: Circle [constr] CenterX=0 CenterY=0 CenterZ=0 NormalX=0 NormalY=0 NormalZ=1 AngleXU=0 Radius=56.5685
    g19: Circle [constr] CenterX=0 CenterY=0 CenterZ=0 NormalX=0 NormalY=0 NormalZ=1 AngleXU=0 Radius=25
    g20: Circle CenterX=-21.6506 CenterY=12.5 CenterZ=0 NormalX=0 NormalY=0 NormalZ=1 AngleXU=0 Radius=1.6
    g21: Circle CenterX=21.6506 CenterY=12.5 CenterZ=0 NormalX=0 NormalY=0 NormalZ=1 AngleXU=0 Radius=1.6
    g22: Circle CenterX=0 CenterY=-25 CenterZ=0 NormalX=0 NormalY=0 NormalZ=1 AngleXU=0 Radius=1.6
    g23: LineSegment [constr] StartX=0 StartY=0 StartZ=0 EndX=21.6506 EndY=12.5 EndZ=0
    g24: LineSegment [constr] StartX=0 StartY=0 StartZ=0 EndX=0 EndY=-25 EndZ=0
    g25: LineSegment [constr] StartX=0 StartY=0 StartZ=0 EndX=-21.6506 EndY=12.5 EndZ=0
    g26: LineSegment StartX=11.547 StartY=20 StartZ=0 EndX=-11.547 EndY=20 EndZ=0
    g27: LineSegment StartX=-11.547 StartY=20 StartZ=0 EndX=-23.094 EndY=1.0409e-12 EndZ=0
    g28: LineSegment StartX=-23.094 StartY=1.0409e-12 StartZ=0 EndX=-11.547 EndY=-20 EndZ=0
    g29: LineSegment StartX=-11.547 StartY=-20 StartZ=0 EndX=11.547 EndY=-20 EndZ=0
    g30: LineSegment StartX=11.547 StartY=-20 StartZ=0 EndX=23.094 EndY=1.0374e-12 EndZ=0
    g31: LineSegment StartX=23.094 StartY=1.0374e-12 StartZ=0 EndX=11.547 EndY=20 EndZ=0
    g32: Circle [constr] CenterX=0 CenterY=0 CenterZ=0 NormalX=0 NormalY=0 NormalZ=1 AngleXU=0 Radius=23.094
  constraints (88):
    c: Coincident(g0,g1)
    c: Horizontal(g1)
    c: Coincident(g1,g2)
    c: Vertical(g2)
    c: Coincident(g2,g3)
    c: Coincident(g3,g4)
    c: Vertical(g4)
    c: Coincident(g4,g5)
    c: Horizontal(g5)
    c: Coincident(g5,g6)
    c: Coincident(g6,g7)
    c: Coincident(g7,g8)
    c: Coincident(g8,g9)
    c: Coincident(g9,g10)
    c: Coincident(g10,g11)
    c: Coincident(g11,g12)
    c: Horizontal(g12)
    c: Coincident(g12,g13)
    c: Coincident(g13,g14)
    c: Coincident(g14,g15)
    c: Coincident(g15,g16)
    c: Coincident(g16,g17)
    c: Coincident(g17,g0)
    c: DistanceY(g-1,g1) = 40
    c: DistanceX(g1,g1) = 9
    c: Equal(g5,g1)
    c: Equal(g1,g17)
    c: Equal(g17,g13)
    c: Equal(g13,g11)
    c: Equal(g11,g7)
    c: Perpendicular(g10,g11)
    c: Perpendicular(g14,g13)
    c: Perpendicular(g15,g14)
    c: Perpendicular(g9,g10)
    c: Perpendicular(g9,g8)
    c: Perpendicular(g8,g7)
    c: Perpendicular(g17,g16)
    c: Perpendicular(g15,g16)
    c: DistanceY(g2,g2) = 6
    c: Equal(g8,g4)
    c: Equal(g4,g16)
    c: Equal(g0,g6)
    c: Equal(g6,g12)
    c: Coincident(g18,g-1)
    c: PointOnObject(g5,g18)
    c: PointOnObject(g6,g18)
    c: PointOnObject(g11,g18)
    c: PointOnObject(g12,g18)
    c: PointOnObject(g0,g18)
    c: PointOnObject(g0,g18)
    c: Symmetric(g3,g2,g-2)
    c: DistanceX(g3,g3) = 62
    c: Angle(g15,g3) = 1.0472
    c: Angle(g3,g9) = 1.0472
    c: Equal(g10,g8)
    c: Coincident(g19,g18)
    c: PointOnObject(g20,g19)
    c: PointOnObject(g21,g19)
    c: PointOnObject(g22,g19)
    c: PointOnObject(g22,g-2)
    c: Coincident(g23,g18)
    c: Coincident(g23,g21)
    c: Coincident(g24,g18)
    c: Coincident(g24,g22)
    c: Coincident(g25,g18)
    c: Coincident(g25,g20)
    c: Angle(g23,g25) = 2.0944
    c: Angle(g24,g23) = 2.0944
    c: DistanceY(g24,g24) = 25
    c: Equal(g21,g22)
    c: Equal(g22,g20)
    c: Diameter(g21) = 3.2
    c: Coincident(g26,g27)
    c: Coincident(g27,g28)
    c: Coincident(g28,g29)
    c: Coincident(g29,g30)
    c: Coincident(g30,g31)
    c: Coincident(g31,g26)
    c: Equal(g26, g27-g31) x5
    c: PointOnObject(g26,g32)
    c: PointOnObject(g27,g32)
    c: PointOnObject(g28,g32)
    c: PointOnObject(g29,g32)
    c: PointOnObject(g30,g32)
    c: PointOnObject(g31,g32)
    c: Coincident(g32,g18)
    c: Horizontal(g26)
    c: DistanceY(g26) = 20
FEATURE [PartDesign::Pad] Pad021
  AddSubType = 0
  AutoTaperInnerAngle = false
  CheckUpToFaceLimits = true
  ClaimChildren = false
  Direction = (1,1,1)
  Fit = 0
  FitJoin = 0
  InnerFit = 0
  InnerFitJoin = 0
  InvalidShape = false
  Length = 5
  Length2 = 100
  Linearize = true
  NewSolid = false
  Profile = -> Sketch034
  Refine = true
  Suppress = false
  TaperInnerAngle = 0
  TaperInnerAngleRev = 0
  TreeRank = 0
  Type = 0
  ValidateShape = true
  _ProfileBasedVersion = 1
FEATURE [PartDesign::Fillet] Fillet012
  AddSubType = 0
  Base = -> Pad021 [Edge59,Edge56,Edge68,Edge55,Edge65,Edge62]
  BaseFeature = -> Pad021
  InvalidShape = false
  NewSolid = false
  Radius = 3
  Refine = true
  SupportTransform = false
  Suppress = false
  TreeRank = 0
  UseAllEdges = false
  ValidateShape = true
FEATURE [PartDesign::Fillet] Fillet013
  AddSubType = 0
  Base = -> Fillet012 [Edge94,Edge93,Edge95,Edge96,Edge81,Edge82,Edge84,Edge83,Edge88,Edge87,Edge86,Edge85,Edge80,Edge79,Edge92,Edge91,Edge90,Edge89]
  BaseFeature = -> Fillet012
  InvalidShape = false
  NewSolid = false
  Radius = 0.5
  Refine = true
  SupportTransform = false
  Suppress = false
  TreeRank = 0
  UseAllEdges = false
  ValidateShape = true
FEATURE [PartDesign::Body] Body020  label="CaleCentrale"
  AutoGroupSolids = false
  ClaimAllChildren = false
  ExportMode = 0
  Group = -> [Sketch034,Pad021,Fillet012,Fillet013]
  InvalidShape = false
  Origin = -> Origin030
  SingleSolid = true
  Tip = -> Fillet013
  TreeRank = 0
  ValidateShape = true
  _ExportChildren = -> [Pad021,Fillet012,Fillet013]
  _GroupVersion = 1
COMPONENT P8 — recipe-attached ("SupportGauche120d", modeled in this document).
Construction recipe (the document's own serialized feature program — sketch geometry with constraints, then the solid features built on it; lengths are millimeters unless a unit is written):

FEATURE [Sketcher::SketchObject] Sketch049
  ArcFitTolerance = 0
  AttachmentSupport = -> [XY_Plane033]
  ExternalBSplineMaxDegree = 0
  ExternalBSplineTolerance = 0
  FullyConstrained = true
  InternalTolerance = 1e-06
  InvalidShape = false
  MakeInternals = false
  MapMode = 5
  Support = -> [XY_Plane033]
  TreeRank = 0
  ValidateShape = true
  sketch-geometry (13):
    g0: LineSegment [constr] StartX=0 StartY=0 StartZ=0 EndX=0 EndY=12.5 EndZ=0
    g1: LineSegment StartX=0 StartY=12.5 StartZ=0 EndX=5 EndY=21.1603 EndZ=0
    g2: LineSegment StartX=5 StartY=21.1603 StartZ=0 EndX=13.6603 EndY=16.1603 EndZ=0
    g3: LineSegment StartX=13.6603 StartY=16.1603 StartZ=0 EndX=4.33013 EndY=0 EndZ=0
    g4: LineSegment StartX=4.33013 StartY=0 StartZ=0 EndX=0 EndY=0 EndZ=0
    g5: LineSegment StartX=0 StartY=12.5 StartZ=0 EndX=-2 EndY=12.5 EndZ=0
    g6: LineSegment StartX=-2 StartY=12.5 StartZ=0 EndX=-2 EndY=10 EndZ=0
    g7: LineSegment StartX=-2 StartY=10 StartZ=0 EndX=0 EndY=10 EndZ=0
    g8: LineSegment StartX=0 StartY=10 StartZ=0 EndX=0 EndY=6.25 EndZ=0
    g9: LineSegment StartX=0 StartY=6.25 StartZ=0 EndX=-2 EndY=6.25 EndZ=0
    g10: LineSegment StartX=-2 StartY=6.25 StartZ=0 EndX=-2 EndY=3.75 EndZ=0
    g11: LineSegment StartX=-2 StartY=3.75 StartZ=0 EndX=0 EndY=3.75 EndZ=0
    g12: LineSegment StartX=0 StartY=3.75 StartZ=0 EndX=0 EndY=0 EndZ=0
  constraints (37):
    c: Coincident(g-1,g0)
    c: PointOnObject(g0,g-2)
    c: Coincident(g1,g2)
    c: Coincident(g2,g3)
    c: PointOnObject(g3,g-1)
    c: Coincident(g3,g4)
    c: Coincident(g4,g0)
    c: Perpendicular(g2,g1)
    c: Perpendicular(g2,g3)
    c: DistanceY(g0,g0) = 12.5
    c: Distance(g2) = 10
    c: Distance(g1) = 10
    c: Horizontal(g5)
    c: Coincident(g6,g5)
    c: Vertical(g6)
    c: Coincident(g7,g6)
    c: PointOnObject(g7,g0)
    c: Horizontal(g7)
    c: Coincident(g8,g7)
    c: PointOnObject(g8,g0)
    c: Coincident(g9,g8)
    c: Coincident(g10,g9)
    c: Coincident(g11,g10)
    c: PointOnObject(g11,g0)
    c: Coincident(g12,g11)
    c: Coincident(g12,g4)
    c: Perpendicular(g10,g9)
    c: Perpendicular(g10,g11)
    c: Parallel(g10,g8)
    c: Equal(g8,g12)
    c: DistanceY(g4,g7) = 10
    c: DistanceY(g10,g10) = 2.5
    c: DistanceX(g9,g9) = 2
    c: DistanceX(g5,g5) = 2
    c: Coincident(g1,g5)
    c: Coincident(g1,g0)
    c: Angle(g1,g5) = 2.0944
FEATURE [PartDesign::Pad] Pad029
  AddSubType = 0
  AutoTaperInnerAngle = false
  CheckUpToFaceLimits = true
  ClaimChildren = false
  Direction = (1,1,1)
  Fit = 0
  FitJoin = 0
  InnerFit = 0
  InnerFitJoin = 0
  InvalidShape = false
  Length = 7
  Length2 = 100
  Linearize = true
  NewSolid = false
  Profile = -> Sketch049
  Refine = true
  Suppress = false
  TaperInnerAngle = 0
  TaperInnerAngleRev = 0
  TreeRank = 0
  Type = 0
  ValidateShape = true
  _ProfileBasedVersion = 1
FEATURE [Sketcher::SketchObject] Sketch051
  ArcFitTolerance = 0
  AttachmentSupport = -> [XY_Plane033]
  ExternalBSplineMaxDegree = 0
  ExternalBSplineTolerance = 0
  ExternalGeometry = -> [Pad029]
  FullyConstrained = true
  InternalTolerance = 1e-06
  InvalidShape = false
  MakeInternals = false
  MapMode = 5
  Support = -> [XY_Plane033]
  TreeRank = 0
  ValidateShape = true
  sketch-geometry (4):
    g0: LineSegment StartX=4.33013 StartY=10 StartZ=0 EndX=4.33013 EndY=0 EndZ=0
    g1: LineSegment StartX=0 StartY=6.25 StartZ=0 EndX=0 EndY=3.75 EndZ=0
    g2: LineSegment StartX=4.33013 StartY=10 StartZ=0 EndX=0 EndY=12.5 EndZ=0
    g3: LineSegment StartX=0 StartY=12.5 StartZ=0 EndX=-2 EndY=12.5 EndZ=0
  constraints (10):
    c: Vertical(g0)
    c: Coincident(g1,g-8)
    c: Coincident(g1,g-5)
    c: Coincident(g0,g-11)
    c: Coincident(g2,g0)
    c: PointOnObject(g2,g-12)
    c: Coincident(g3,g-10)
    c: Coincident(g2,g3)
    c: Horizontal(g3)
    c: Perpendicular(g-12,g2)
FEATURE [PartDesign::Pad] Pad030
  AddSubType = 0
  AutoTaperInnerAngle = false
  BaseFeature = -> Pad029
  CheckUpToFaceLimits = true
  ClaimChildren = false
  Direction = (1,1,1)
  Fit = 0
  FitJoin = 0
  InnerFit = 0
  InnerFitJoin = 0
  InvalidShape = false
  Length = 15
  Length2 = 100
  Linearize = true
  NewSolid = false
  Profile = -> Sketch051
  Refine = true
  Reversed = true
  Suppress = false
  TaperInnerAngle = 0
  TaperInnerAngleRev = 0
  TreeRank = 0
  Type = 0
  ValidateShape = true
  _ProfileBasedVersion = 1
FEATURE [Sketcher::SketchObject] Sketch052
  ArcFitTolerance = 0
  AttachmentSupport = -> [YZ_Plane033]
  ExternalBSplineMaxDegree = 0
  ExternalBSplineTolerance = 0
  ExternalGeometry = -> [Pad030]
  FullyConstrained = true
  InternalTolerance = 1e-06
  InvalidShape = false
  MakeInternals = false
  MapMode = 5
  Placement = pos=(0,0,0) rot=(0.57735,0.57735,0.57735;2.0944rad)
  Support = -> [YZ_Plane033]
  TreeRank = 0
  ValidateShape = true
  sketch-geometry (1):
    g0: Circle CenterX=5 CenterY=-10 CenterZ=0 NormalX=0 NormalY=0 NormalZ=1 AngleXU=0 Radius=1.6
  constraints (3):
    c: DistanceX(g0) = 5
    c: Diameter(g0) = 3.2
    c: DistanceY(g-3,g0) = 5
FEATURE [PartDesign::Pocket] Pocket020
  AddSubType = 1
  AutoTaperInnerAngle = false
  BaseFeature = -> Pad030
  CheckUpToFaceLimits = true
  ClaimChildren = false
  Direction = (1,1,1)
  Fit = 0
  FitJoin = 0
  InnerFit = 0
  InnerFitJoin = 0
  InvalidShape = false
  Length = 5
  Length2 = 100
  Linearize = true
  NewSolid = false
  Profile = -> Sketch052
  Refine = true
  Reversed = true
  Suppress = false
  TaperInnerAngle = 0
  TaperInnerAngleRev = 0
  TreeRank = 0
  Type = 1
  ValidateShape = true
  _ProfileBasedVersion = 1
  _Version = 0
FEATURE [Sketcher::SketchObject] Sketch054
  ArcFitTolerance = 0
  AttachmentSupport = -> [XY_Plane033]
  ExternalBSplineMaxDegree = 0
  ExternalBSplineTolerance = 0
  ExternalGeometry = -> [Pocket020]
  FullyConstrained = true
  InternalTolerance = 1e-06
  InvalidShape = false
  MakeInternals = false
  MapMode = 5
  Support = -> [XY_Plane033]
  TreeRank = 0
  ValidateShape = true
  sketch-geometry (3):
    g0: Circle CenterX=6.83013 CenterY=14.3301 CenterZ=0 NormalX=0 NormalY=0 NormalZ=1 AngleXU=0 Radius=2.1
    g1: LineSegment [constr] StartX=9.33013 StartY=18.6603 StartZ=0 EndX=6.83013 EndY=14.3301 EndZ=0
    g2: LineSegment [constr] StartX=6.83013 StartY=14.3301 StartZ=0 EndX=11.1603 EndY=11.8301 EndZ=0
  constraints (11):
    c: Diameter(g0) = 4.2
    c: Coincident(g1,g0)
    c: Coincident(g1,g2)
    c: Perpendicular(g1,g2)
    c: Distance(g1) = 5
    c: Distance(g2) = 5
    c: PointOnObject(g2,g-4)
    c: PointOnObject(g1,g-3)
    c: Perpendicular(g-3,g1)
    c: DistanceX(g-1,g0) = 6.83013
    c: DistanceY(g-1,g0) = 14.3301
FEATURE [PartDesign::Pocket] Pocket022
  AddSubType = 1
  AutoTaperInnerAngle = false
  BaseFeature = -> Pocket020
  CheckUpToFaceLimits = true
  ClaimChildren = false
  Direction = (1,1,1)
  Fit = 0
  FitJoin = 0
  InnerFit = 0
  InnerFitJoin = 0
  InvalidShape = false
  Length = 5
  Length2 = 100
  Linearize = true
  NewSolid = false
  Profile = -> Sketch054
  Refine = true
  Reversed = true
  Suppress = false
  TaperInnerAngle = 0
  TaperInnerAngleRev = 0
  TreeRank = 0
  Type = 1
  ValidateShape = true
  _ProfileBasedVersion = 1
  _Version = 0
FEATURE [Sketcher::SketchObject] Sketch055
  ArcFitTolerance = 0
  AttachmentSupport = -> [Pocket022]
  ExternalBSplineMaxDegree = 0
  ExternalBSplineTolerance = 0
  ExternalGeometry = -> [Pocket022]
  FullyConstrained = true
  InternalTolerance = 1e-06
  InvalidShape = false
  MakeInternals = false
  MapMode = 5
  Placement = pos=(4.33013,0,0) rot=(0.57735,0.57735,0.57735;2.0944rad)
  Support = -> [Pocket022]
  TreeRank = 0
  ValidateShape = true
  sketch-geometry (4):
    g0: LineSegment StartX=0 StartY=-15 StartZ=0 EndX=12.5 EndY=-15 EndZ=0
    g1: LineSegment StartX=12.5 StartY=-15 StartZ=0 EndX=12.5 EndY=-5 EndZ=0
    g2: LineSegment StartX=12.5 StartY=-5 StartZ=0 EndX=0 EndY=-5 EndZ=0
    g3: LineSegment StartX=0 StartY=-5 StartZ=0 EndX=0 EndY=-15 EndZ=0
  constraints (11):
    c: Coincident(g0,g1)
    c: Coincident(g1,g2)
    c: Coincident(g2,g3)
    c: Coincident(g3,g0)
    c: Horizontal(g0)
    c: Horizontal(g2)
    c: Vertical(g1)
    c: Vertical(g3)
    c: PointOnObject(g1,g-4)
    c: Coincident(g0,g-3)
    c: DistanceY(g3,g3) = 10
FEATURE [PartDesign::Pocket] Pocket023
  AddSubType = 1
  AutoTaperInnerAngle = false
  BaseFeature = -> Pocket022
  CheckUpToFaceLimits = true
  ClaimChildren = false
  Direction = (1,1,1)
  Fit = 0
  FitJoin = 0
  InnerFit = 0
  InnerFitJoin = 0
  InvalidShape = false
  Length = 1.9
  Length2 = 100
  Linearize = true
  NewSolid = false
  Profile = -> Sketch055
  Refine = true
  Suppress = false
  TaperInnerAngle = 0
  TaperInnerAngleRev = 0
  TreeRank = 0
  Type = 0
  ValidateShape = true
  _ProfileBasedVersion = 1
  _Version = 0
FEATURE [Sketcher::SketchObject] Sketch056
  ArcFitTolerance = 0
  AttachmentSupport = -> [XY_Plane033]
  ExternalBSplineMaxDegree = 0
  ExternalBSplineTolerance = 0
  ExternalGeometry = -> [Pocket023]
  FullyConstrained = true
  InternalTolerance = 1e-06
  InvalidShape = false
  MakeInternals = false
  MapMode = 5
  Support = -> [XY_Plane033]
  TreeRank = 0
  ValidateShape = true
  sketch-geometry (3):
    g0: LineSegment StartX=4.33013 StartY=10 StartZ=0 EndX=4.33013 EndY=0 EndZ=0
    g1: LineSegment StartX=4.33013 StartY=0 StartZ=0 EndX=8.66025 EndY=7.5 EndZ=0
    g2: LineSegment StartX=8.66025 StartY=7.5 StartZ=0 EndX=4.33013 EndY=10 EndZ=0
  constraints (7):
    c: Coincident(g-5,g0)
    c: Coincident(g0,g-4)
    c: Coincident(g0,g1)
    c: PointOnObject(g1,g-4)
    c: Coincident(g1,g2)
    c: Coincident(g2,g0)
    c: Parallel(g2,g-5)
FEATURE [PartDesign::Pad] Pad031
  AddSubType = 0
  AutoTaperInnerAngle = false
  BaseFeature = -> Pocket023
  CheckUpToFaceLimits = true
  ClaimChildren = false
  Direction = (1,1,1)
  Fit = 0
  FitJoin = 0
  InnerFit = 0
  InnerFitJoin = 0
  InvalidShape = false
  Length = 10
  Length2 = 100
  Linearize = true
  NewSolid = false
  Profile = -> Sketch056
  Refine = true
  Reversed = true
  Suppress = false
  TaperInnerAngle = 0
  TaperInnerAngleRev = 0
  TreeRank = 0
  Type = 3
  UpToFace = -> Pocket023 [Face19]
  ValidateShape = true
  _ProfileBasedVersion = 1
FEATURE [PartDesign::Draft] Draft
  AddSubType = 0
  Angle = 38.5
  Base = -> Pad031 [Face20]
  BaseFeature = -> Pad031
  InvalidShape = false
  NeutralPlane = -> Pad031 [Face15]
  NewSolid = false
  Refine = true
  SupportTransform = false
  Suppress = false
  TreeRank = 0
  ValidateShape = true
FEATURE [PartDesign::Chamfer] Chamfer009
  AddSubType = 0
  Angle = 45
  Base = -> Draft [Edge26]
  BaseFeature = -> Draft
  ChamferType = 0
  FlipDirection = false
  InvalidShape = false
  NewSolid = false
  Refine = true
  Size = 2
  Size2 = 1
  SupportTransform = false
  Suppress = false
  TreeRank = 0
  UseAllEdges = false
  ValidateShape = true
FEATURE [PartDesign::Draft] Draft001
  AddSubType = 0
  Angle = 66.5
  Base = -> Chamfer009 [Face16]
  BaseFeature = -> Chamfer009
  InvalidShape = false
  NeutralPlane = -> Chamfer009 [Face21]
  NewSolid = false
  Refine = true
  Reversed = true
  SupportTransform = false
  Suppress = false
  TreeRank = 0
  ValidateShape = true
FEATURE [PartDesign::Chamfer] Chamfer010
  AddSubType = 0
  Angle = 45
  Base = -> Draft001 [Edge51,Edge50,Edge54,Edge53]
  BaseFeature = -> Draft001
  ChamferType = 0
  FlipDirection = false
  InvalidShape = false
  NewSolid = false
  Refine = true
  Size = 0.4
  Size2 = 1
  SupportTransform = false
  Suppress = false
  TreeRank = 0
  UseAllEdges = false
  ValidateShape = true
FEATURE [PartDesign::Chamfer] Chamfer011
  AddSubType = 0
  Angle = 45
  Base = -> Chamfer010 [Edge45]
  BaseFeature = -> Chamfer010
  ChamferType = 0
  FlipDirection = false
  InvalidShape = false
  NewSolid = false
  Refine = true
  Size = 1
  Size2 = 1
  SupportTransform = false
  Suppress = false
  TreeRank = 0
  UseAllEdges = false
  ValidateShape = true
FEATURE [PartDesign::Chamfer] Chamfer012
  AddSubType = 0
  Angle = 45
  Base = -> Chamfer011 [Edge10,Edge19]
  BaseFeature = -> Chamfer011
  ChamferType = 0
  FlipDirection = false
  InvalidShape = false
  NewSolid = false
  Refine = true
  Size = 0.2
  Size2 = 1
  SupportTransform = false
  Suppress = false
  TreeRank = 0
  UseAllEdges = false
  ValidateShape = true
FEATURE [PartDesign::Chamfer] Chamfer013
  AddSubType = 0
  Angle = 45
  Base = -> Chamfer012 [Edge64,Edge38]
  BaseFeature = -> Chamfer012
  ChamferType = 0
  FlipDirection = false
  InvalidShape = false
  NewSolid = false
  Refine = true
  Size = 1
  Size2 = 1
  SupportTransform = false
  Suppress = false
  TreeRank = 0
  UseAllEdges = false
  ValidateShape = true
FEATURE [PartDesign::Fillet] Fillet016
  AddSubType = 0
  Base = -> Chamfer013 [Edge37]
  BaseFeature = -> Chamfer013
  InvalidShape = false
  NewSolid = false
  Radius = 2
  Refine = true
  SupportTransform = false
  Suppress = false
  TreeRank = 0
  UseAllEdges = false
  ValidateShape = true
FEATURE [PartDesign::Chamfer] Chamfer014
  AddSubType = 0
  Angle = 45
  Base = -> Fillet016 [Edge20,Edge70,Edge79,Edge44]
  BaseFeature = -> Fillet016
  ChamferType = 0
  FlipDirection = false
  InvalidShape = false
  NewSolid = false
  Refine = true
  Size = 0.2
  Size2 = 1
  SupportTransform = false
  Suppress = false
  TreeRank = 0
  UseAllEdges = false
  ValidateShape = true
FEATURE [Sketcher::SketchObject] Sketch057
  ArcFitTolerance = 0
  AttachmentSupport = -> [XY_Plane033]
  ExternalBSplineMaxDegree = 0
  ExternalBSplineTolerance = 0
  FullyConstrained = false
  InternalTolerance = 1e-06
  InvalidShape = false
  MakeInternals = false
  MapMode = 5
  Support = -> [XY_Plane033]
  TreeRank = 0
  ValidateShape = true
  sketch-geometry (4):
    g0: LineSegment StartX=0 StartY=15.6465 StartZ=0 EndX=-3.55109 EndY=15.6465 EndZ=0
    g1: LineSegment StartX=-3.55109 StartY=15.6465 StartZ=0 EndX=-3.55109 EndY=7.42705 EndZ=0
    g2: LineSegment StartX=-3.55109 StartY=7.42705 StartZ=0 EndX=0 EndY=7.42705 EndZ=0
    g3: LineSegment StartX=0 StartY=7.42705 StartZ=0 EndX=0 EndY=15.6465 EndZ=0
  constraints (9):
    c: Coincident(g0,g1)
    c: Coincident(g1,g2)
    c: Coincident(g2,g3)
    c: Coincident(g3,g0)
    c: Horizontal(g0)
    c: Horizontal(g2)
    c: Vertical(g1)
    c: Vertical(g3)
    c: PointOnObject(g0,g-2)
FEATURE [PartDesign::Pocket] Pocket024
  AddSubType = 1
  AutoTaperInnerAngle = false
  BaseFeature = -> Chamfer014
  CheckUpToFaceLimits = true
  ClaimChildren = false
  Direction = (1,1,1)
  Fit = 0
  FitJoin = 0
  InnerFit = 0
  InnerFitJoin = 0
  InvalidShape = false
  Length = 39
  Length2 = 100
  Linearize = true
  Midplane = true
  NewSolid = false
  Profile = -> Sketch057
  Refine = true
  Suppress = false
  TaperInnerAngle = 0
  TaperInnerAngleRev = 0
  TreeRank = 0
  Type = 1
  ValidateShape = true
  _ProfileBasedVersion = 1
  _Version = 0
FEATURE [PartDesign::Chamfer] Chamfer015
  AddSubType = 0
  Angle = 45
  Base = -> Pocket024 [Edge69,Edge58,Edge54]
  BaseFeature = -> Pocket024
  ChamferType = 0
  FlipDirection = false
  InvalidShape = false
  NewSolid = false
  Refine = true
  Size = 0.5
  Size2 = 1
  SupportTransform = false
  Suppress = false
  TreeRank = 0
  UseAllEdges = false
  ValidateShape = true
FEATURE [PartDesign::Body] Body026
  AutoGroupSolids = false
  ClaimAllChildren = false
  ExportMode = 0
  Group = -> [Sketch049,Sketch051,Sketch052,Sketch054,Pad029,Pad030,Pocket020,Pocket022,Sketch055,Pocket023,Sketch056,Pad031,Draft,Chamfer009,Draft001,Chamfer010,Chamfer011,Chamfer012,Chamfer013,Fillet016,Chamfer014,Sketch057,Pocket024,Chamfer015]
  InvalidShape = false
  Origin = -> Origin041
  SingleSolid = true
  Tip = -> Chamfer015
  TreeRank = 0
  ValidateShape = true
  _ExportChildren = -> [Pad029,Pad030,Pocket020,Pocket022,Pocket023,Pad031,Draft,Chamfer009,Draft001,Chamfer010,Chamfer011,Chamfer012,Chamfer013,Fillet016,Chamfer014,Pocket024,Chamfer015]
  _GroupVersion = 1
COMPONENT P9 — geometry summary ("SupportDroite120d"; no construction recipe available for this part):
  bounding box: 22.0 x 20.7 x 15.2 mm
  tessellated surface: 2,216 triangles
  volume: 1668 mm^3 (24% of its bounding box)
COMPONENT P10 — recipe-attached ("CoinBAU", modeled in this document).
Construction recipe (the document's own serialized feature program — sketch geometry with constraints, then the solid features built on it; lengths are millimeters unless a unit is written):

FEATURE [PartDesign::SubShapeBinder] Binder  label="Binder(Chamfer023)"
  BindCopyOnChange = 0
  BindMode = 0
  ClaimChildren = false
  Context = -> Part010 [Body030.Binder.]
  EdgeTolerance = 1e-06
  FillStyle = 0
  Fuse = false
  InvalidShape = false
  MakeFace = true
  MergeEdges = true
  OffsetFill = false
  OffsetIntersection = false
  OffsetJoinType = 0
  OffsetOpenResult = false
  Outline = false
  PartialLoad = false
  Refine = true
  Relative = true
  SplitEdges = false
  Support = -> [Chamfer023[Face30]]
  TightBound = false
  TreeRank = 0
  ValidateShape = true
  _Version = 8
FEATURE [Sketcher::SketchObject] Sketch067
  ArcFitTolerance = 0
  AttachmentSupport = -> [Binder]
  ExternalBSplineMaxDegree = 0
  ExternalBSplineTolerance = 0
  ExternalGeometry = -> [Binder]
  FullyConstrained = true
  InternalTolerance = 1e-06
  InvalidShape = false
  MakeInternals = false
  MapMode = 5
  Placement = pos=(-2.82e-14,-50.4105,60.0769) rot=(1,0,0;0.698132rad)
  Support = -> [Binder]
  TreeRank = 0
  ValidateShape = true
  sketch-geometry (3):
    g0: Circle CenterX=-2e-16 CenterY=-32.5627 CenterZ=0 NormalX=0 NormalY=0 NormalZ=1 AngleXU=0 Radius=8
    g1: Circle CenterX=14 CenterY=-14.7181 CenterZ=0 NormalX=0 NormalY=0 NormalZ=1 AngleXU=0 Radius=1.6
    g2: Circle CenterX=-14 CenterY=-14.7181 CenterZ=0 NormalX=0 NormalY=0 NormalZ=1 AngleXU=0 Radius=1.6
  constraints (6):
    c: Coincident(g0,g-9)
    c: Diameter(g0) = 16
    c: Coincident(g1,g-10)
    c: Coincident(g2,g-11)
    c: Diameter(g2) = 3.2
    c: Equal(g2,g1)
FEATURE [PartDesign::Pad] Pad035
  AddSubType = 0
  AutoTaperInnerAngle = false
  CheckUpToFaceLimits = true
  ClaimChildren = false
  Direction = (-4e-16,-0.642788,0.766044)
  Fit = 0
  FitJoin = 0
  InnerFit = 0
  InnerFitJoin = 0
  InvalidShape = false
  Length = 3
  Length2 = 100
  Linearize = true
  NewSolid = false
  Profile = -> Sketch067
  Refine = true
  Suppress = false
  TaperInnerAngle = 0
  TaperInnerAngleRev = 0
  TreeRank = 0
  Type = 0
  ValidateShape = true
  _ProfileBasedVersion = 1
FEATURE [PartDesign::Chamfer] Chamfer021
  AddSubType = 0
  Angle = 45
  Base = -> Pad035 [Edge8,Edge11,Edge5,Edge1,Edge14,Edge2]
  BaseFeature = -> Pad035
  ChamferType = 0
  FlipDirection = false
  InvalidShape = false
  NewSolid = false
  Refine = true
  Size = 0.4
  Size2 = 1
  SupportTransform = false
  Suppress = false
  TreeRank = 0
  UseAllEdges = false
  ValidateShape = true
FEATURE [PartDesign::Body] Body030  label="PlateBAU"
  AutoGroupSolids = false
  ClaimAllChildren = false
  ExportMode = 0
  Group = -> [Binder,Sketch067,Pad035,Chamfer021]
  InvalidShape = false
  Origin = -> Origin048
  SingleSolid = true
  Tip = -> Chamfer021
  TreeRank = 0
  ValidateShape = true
  _ExportChildren = -> [Binder,Pad035,Chamfer021]
  _GroupVersion = 1
